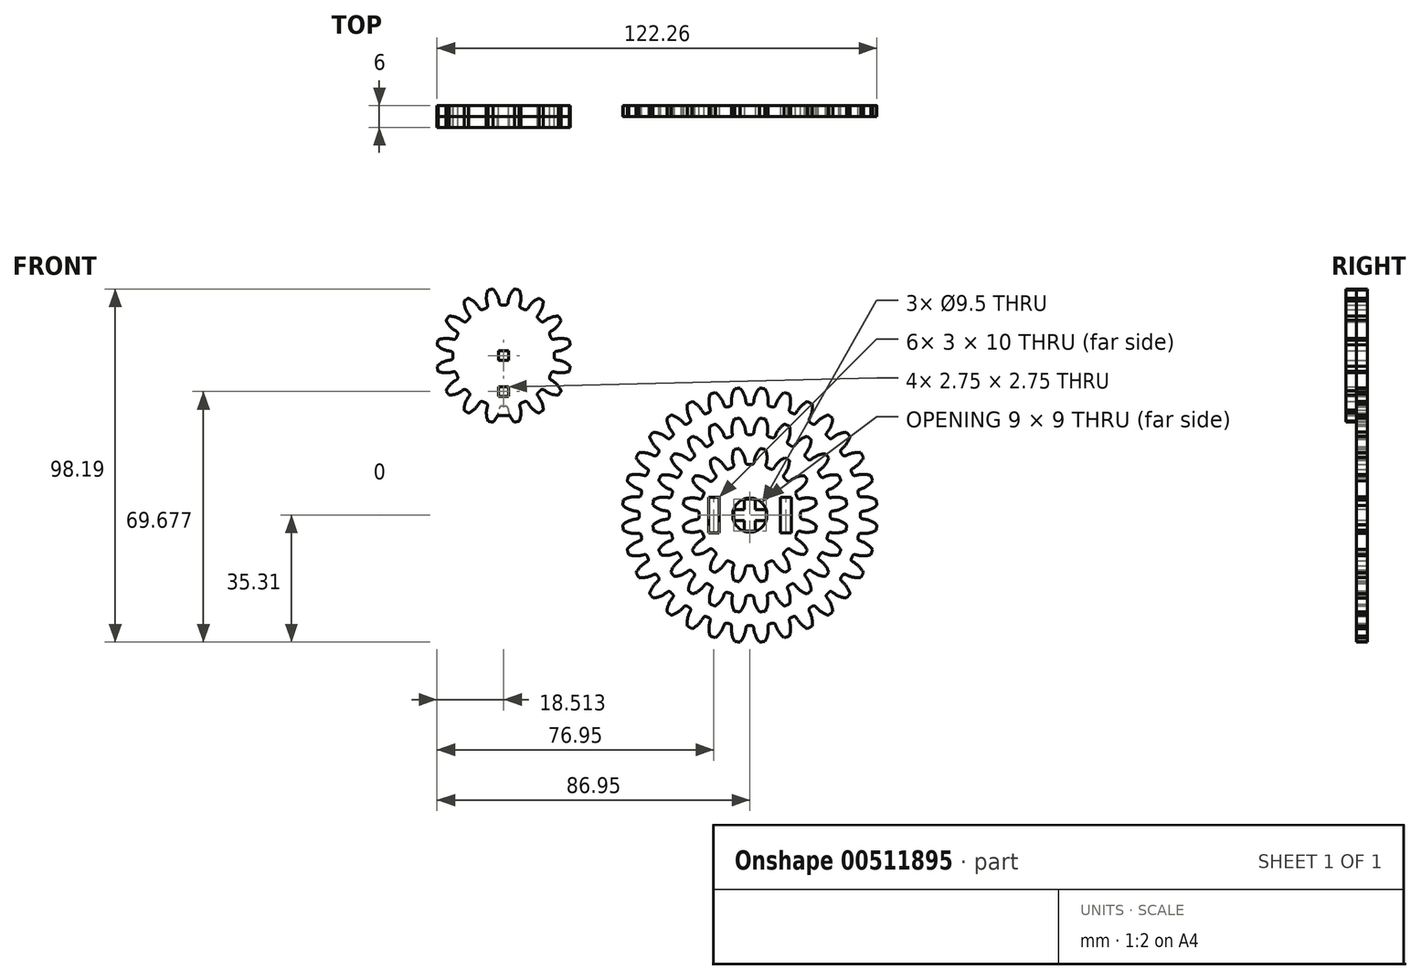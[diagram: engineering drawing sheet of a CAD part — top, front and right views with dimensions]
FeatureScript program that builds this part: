
annotation { "Feature Type Name" : "Feature", "Feature Type Description" : "" }
export const myFeature = defineFeature(function(context is Context, id is Id, definition is map)
    precondition{}
    {
        {
            var Q0;
            Q0=qCreatedBy(makeId("Front.planeOp"),FACE);
            var sketch = newSketch(context, id + "F0", { "sketchPlane" : qUnion([Q0])});
            skArc(sketch, "E0.0", {"start": v(4.27, 26.74) * mm, "mid": v(3.54, 26.85) * mm, "end": v(2.8, 26.94) * mm});
            skArc(sketch, "E1.0", {"start": v(5.4, 21.73) * mm, "mid": v(4.95, 22.07) * mm, "end": v(4.85, 22.62) * mm});
            skArc(sketch, "E2.0", {"start": v(6.18, 21.53) * mm, "mid": v(5.8, 21.63) * mm, "end": v(5.4, 21.73) * mm});
            skArc(sketch, "E3.0", {"start": v(7.1, 22.02) * mm, "mid": v(6.74, 21.58) * mm, "end": v(6.18, 21.53) * mm});
            skPoint(sketch, "E4.0", {"position": v(9.67, 25.3) * mm});
            skArc(sketch, "E5", {"start": v(4.85, 22.62) * mm, "mid": v(4.93, 24.74) * mm, "end": v(4.27, 26.74) * mm});
            skArc(sketch, "E6", {"start": v(7.1, 22.02) * mm, "mid": v(8.1, 23.89) * mm, "end": v(9.67, 25.3) * mm});
            skArc(sketch, "E7.1.0", {"start": v(11.54, 19.2) * mm, "mid": v(11.2, 19.4) * mm, "end": v(10.85, 19.6) * mm});
            skArc(sketch, "E7.1.1", {"start": v(10.85, 19.6) * mm, "mid": v(10.5, 20.03) * mm, "end": v(10.54, 20.6) * mm});
            skPoint(sketch, "E7.1.2", {"position": v(15.9, 21.93) * mm});
            skArc(sketch, "E7.1.3", {"start": v(12.56, 19.43) * mm, "mid": v(12.1, 19.1) * mm, "end": v(11.54, 19.2) * mm});
            skArc(sketch, "E7.1.4", {"start": v(12.56, 19.43) * mm, "mid": v(14, 20.98) * mm, "end": v(15.9, 21.93) * mm});
            skArc(sketch, "E7.1.5", {"start": v(10.54, 20.6) * mm, "mid": v(11.16, 22.62) * mm, "end": v(11.05, 24.73) * mm});
            skArc(sketch, "E7.1.6", {"start": v(11.05, 24.73) * mm, "mid": v(10.36, 25.02) * mm, "end": v(9.67, 25.3) * mm});
            skArc(sketch, "E7.2.0", {"start": v(16.12, 15.55) * mm, "mid": v(15.84, 15.84) * mm, "end": v(15.55, 16.12) * mm});
            skArc(sketch, "E7.2.1", {"start": v(15.55, 16.12) * mm, "mid": v(15.32, 16.63) * mm, "end": v(15.52, 17.16) * mm});
            skPoint(sketch, "E7.2.2", {"position": v(21.03, 17.07) * mm});
            skArc(sketch, "E7.2.3", {"start": v(17.16, 15.52) * mm, "mid": v(16.63, 15.32) * mm, "end": v(16.12, 15.55) * mm});
            skArc(sketch, "E7.2.4", {"start": v(17.16, 15.52) * mm, "mid": v(18.96, 16.64) * mm, "end": v(21.03, 17.07) * mm});
            skArc(sketch, "E7.2.5", {"start": v(15.52, 17.16) * mm, "mid": v(16.64, 18.96) * mm, "end": v(17.07, 21.03) * mm});
            skArc(sketch, "E7.2.6", {"start": v(17.07, 21.03) * mm, "mid": v(16.49, 21.49) * mm, "end": v(15.9, 21.93) * mm});
            skArc(sketch, "E7.3.0", {"start": v(19.6, 10.85) * mm, "mid": v(19.4, 11.2) * mm, "end": v(19.2, 11.54) * mm});
            skArc(sketch, "E7.3.1", {"start": v(19.2, 11.54) * mm, "mid": v(19.1, 12.1) * mm, "end": v(19.43, 12.56) * mm});
            skPoint(sketch, "E7.3.2", {"position": v(24.73, 11.05) * mm});
            skArc(sketch, "E7.3.3", {"start": v(20.6, 10.54) * mm, "mid": v(20.03, 10.5) * mm, "end": v(19.6, 10.85) * mm});
            skArc(sketch, "E7.3.4", {"start": v(20.6, 10.54) * mm, "mid": v(22.62, 11.16) * mm, "end": v(24.73, 11.05) * mm});
            skArc(sketch, "E7.3.5", {"start": v(19.43, 12.56) * mm, "mid": v(20.98, 14) * mm, "end": v(21.93, 15.9) * mm});
            skArc(sketch, "E7.3.6", {"start": v(21.93, 15.9) * mm, "mid": v(21.49, 16.49) * mm, "end": v(21.03, 17.07) * mm});
            skArc(sketch, "E7.4.0", {"start": v(21.73, 5.4) * mm, "mid": v(21.63, 5.8) * mm, "end": v(21.53, 6.18) * mm});
            skArc(sketch, "E7.4.1", {"start": v(21.53, 6.18) * mm, "mid": v(21.58, 6.74) * mm, "end": v(22.02, 7.1) * mm});
            skPoint(sketch, "E7.4.2", {"position": v(26.74, 4.27) * mm});
            skArc(sketch, "E7.4.3", {"start": v(22.62, 4.85) * mm, "mid": v(22.07, 4.95) * mm, "end": v(21.73, 5.4) * mm});
            skArc(sketch, "E7.4.4", {"start": v(22.62, 4.85) * mm, "mid": v(24.74, 4.93) * mm, "end": v(26.74, 4.27) * mm});
            skArc(sketch, "E7.4.5", {"start": v(22.02, 7.1) * mm, "mid": v(23.89, 8.1) * mm, "end": v(25.3, 9.67) * mm});
            skArc(sketch, "E7.4.6", {"start": v(25.3, 9.67) * mm, "mid": v(25.02, 10.36) * mm, "end": v(24.73, 11.05) * mm});
            skArc(sketch, "E7.5.0", {"start": v(22.4, -0.4) * mm, "mid": v(22.4, 0) * mm, "end": v(22.4, 0.4) * mm});
            skArc(sketch, "E7.5.1", {"start": v(22.4, 0.4) * mm, "mid": v(22.6, 0.93) * mm, "end": v(23.1, 1.17) * mm});
            skPoint(sketch, "E7.5.2", {"position": v(26.94, -2.8) * mm});
            skArc(sketch, "E7.5.3", {"start": v(23.1, -1.17) * mm, "mid": v(22.6, -0.93) * mm, "end": v(22.4, -0.4) * mm});
            skArc(sketch, "E7.5.4", {"start": v(23.1, -1.17) * mm, "mid": v(25.17, -1.64) * mm, "end": v(26.94, -2.8) * mm});
            skArc(sketch, "E7.5.5", {"start": v(23.1, 1.17) * mm, "mid": v(25.17, 1.64) * mm, "end": v(26.94, 2.8) * mm});
            skArc(sketch, "E7.5.6", {"start": v(26.94, 2.8) * mm, "mid": v(26.85, 3.54) * mm, "end": v(26.74, 4.27) * mm});
            skArc(sketch, "E7.6.0", {"start": v(21.53, -6.18) * mm, "mid": v(21.63, -5.8) * mm, "end": v(21.73, -5.4) * mm});
            skArc(sketch, "E7.6.1", {"start": v(21.73, -5.4) * mm, "mid": v(22.07, -4.95) * mm, "end": v(22.62, -4.85) * mm});
            skPoint(sketch, "E7.6.2", {"position": v(25.3, -9.67) * mm});
            skArc(sketch, "E7.6.3", {"start": v(22.02, -7.1) * mm, "mid": v(21.58, -6.74) * mm, "end": v(21.53, -6.18) * mm});
            skArc(sketch, "E7.6.4", {"start": v(22.02, -7.1) * mm, "mid": v(23.89, -8.1) * mm, "end": v(25.3, -9.67) * mm});
            skArc(sketch, "E7.6.5", {"start": v(22.62, -4.85) * mm, "mid": v(24.74, -4.93) * mm, "end": v(26.74, -4.27) * mm});
            skArc(sketch, "E7.6.6", {"start": v(26.74, -4.27) * mm, "mid": v(26.85, -3.54) * mm, "end": v(26.94, -2.8) * mm});
            skArc(sketch, "E7.7.0", {"start": v(19.2, -11.54) * mm, "mid": v(19.4, -11.2) * mm, "end": v(19.6, -10.85) * mm});
            skArc(sketch, "E7.7.1", {"start": v(19.6, -10.85) * mm, "mid": v(20.03, -10.5) * mm, "end": v(20.6, -10.54) * mm});
            skPoint(sketch, "E7.7.2", {"position": v(21.93, -15.9) * mm});
            skArc(sketch, "E7.7.3", {"start": v(19.43, -12.56) * mm, "mid": v(19.1, -12.1) * mm, "end": v(19.2, -11.54) * mm});
            skArc(sketch, "E7.7.4", {"start": v(19.43, -12.56) * mm, "mid": v(20.98, -14) * mm, "end": v(21.93, -15.9) * mm});
            skArc(sketch, "E7.7.5", {"start": v(20.6, -10.54) * mm, "mid": v(22.62, -11.16) * mm, "end": v(24.73, -11.05) * mm});
            skArc(sketch, "E7.7.6", {"start": v(24.73, -11.05) * mm, "mid": v(25.02, -10.36) * mm, "end": v(25.3, -9.67) * mm});
            skArc(sketch, "E7.8.0", {"start": v(15.55, -16.12) * mm, "mid": v(15.84, -15.84) * mm, "end": v(16.12, -15.55) * mm});
            skArc(sketch, "E7.8.1", {"start": v(16.12, -15.55) * mm, "mid": v(16.63, -15.32) * mm, "end": v(17.16, -15.52) * mm});
            skPoint(sketch, "E7.8.2", {"position": v(17.07, -21.03) * mm});
            skArc(sketch, "E7.8.3", {"start": v(15.52, -17.16) * mm, "mid": v(15.32, -16.63) * mm, "end": v(15.55, -16.12) * mm});
            skArc(sketch, "E7.8.4", {"start": v(15.52, -17.16) * mm, "mid": v(16.64, -18.96) * mm, "end": v(17.07, -21.03) * mm});
            skArc(sketch, "E7.8.5", {"start": v(17.16, -15.52) * mm, "mid": v(18.96, -16.64) * mm, "end": v(21.03, -17.07) * mm});
            skArc(sketch, "E7.8.6", {"start": v(21.03, -17.07) * mm, "mid": v(21.49, -16.49) * mm, "end": v(21.93, -15.9) * mm});
            skArc(sketch, "E7.9.0", {"start": v(10.85, -19.6) * mm, "mid": v(11.2, -19.4) * mm, "end": v(11.54, -19.2) * mm});
            skArc(sketch, "E7.9.1", {"start": v(11.54, -19.2) * mm, "mid": v(12.1, -19.1) * mm, "end": v(12.56, -19.43) * mm});
            skPoint(sketch, "E7.9.2", {"position": v(11.05, -24.73) * mm});
            skArc(sketch, "E7.9.3", {"start": v(10.54, -20.6) * mm, "mid": v(10.5, -20.03) * mm, "end": v(10.85, -19.6) * mm});
            skArc(sketch, "E7.9.4", {"start": v(10.54, -20.6) * mm, "mid": v(11.16, -22.62) * mm, "end": v(11.05, -24.73) * mm});
            skArc(sketch, "E7.9.5", {"start": v(12.56, -19.43) * mm, "mid": v(14, -20.98) * mm, "end": v(15.9, -21.93) * mm});
            skArc(sketch, "E7.9.6", {"start": v(15.9, -21.93) * mm, "mid": v(16.49, -21.49) * mm, "end": v(17.07, -21.03) * mm});
            skArc(sketch, "E7.10.0", {"start": v(5.4, -21.73) * mm, "mid": v(5.8, -21.63) * mm, "end": v(6.18, -21.53) * mm});
            skArc(sketch, "E7.10.1", {"start": v(6.18, -21.53) * mm, "mid": v(6.74, -21.58) * mm, "end": v(7.1, -22.02) * mm});
            skPoint(sketch, "E7.10.2", {"position": v(4.27, -26.74) * mm});
            skArc(sketch, "E7.10.3", {"start": v(4.85, -22.62) * mm, "mid": v(4.95, -22.07) * mm, "end": v(5.4, -21.73) * mm});
            skArc(sketch, "E7.10.4", {"start": v(4.85, -22.62) * mm, "mid": v(4.93, -24.74) * mm, "end": v(4.27, -26.74) * mm});
            skArc(sketch, "E7.10.5", {"start": v(7.1, -22.02) * mm, "mid": v(8.1, -23.89) * mm, "end": v(9.67, -25.3) * mm});
            skArc(sketch, "E7.10.6", {"start": v(9.67, -25.3) * mm, "mid": v(10.36, -25.02) * mm, "end": v(11.05, -24.73) * mm});
            skArc(sketch, "E7.11.0", {"start": v(-0.4, -22.4) * mm, "mid": v(0, -22.4) * mm, "end": v(0.4, -22.4) * mm});
            skArc(sketch, "E7.11.1", {"start": v(0.4, -22.4) * mm, "mid": v(0.93, -22.6) * mm, "end": v(1.17, -23.1) * mm});
            skPoint(sketch, "E7.11.2", {"position": v(-2.8, -26.94) * mm});
            skArc(sketch, "E7.11.3", {"start": v(-1.17, -23.1) * mm, "mid": v(-0.93, -22.6) * mm, "end": v(-0.4, -22.4) * mm});
            skArc(sketch, "E7.11.4", {"start": v(-1.17, -23.1) * mm, "mid": v(-1.64, -25.17) * mm, "end": v(-2.8, -26.94) * mm});
            skArc(sketch, "E7.11.5", {"start": v(1.17, -23.1) * mm, "mid": v(1.64, -25.17) * mm, "end": v(2.8, -26.94) * mm});
            skArc(sketch, "E7.11.6", {"start": v(2.8, -26.94) * mm, "mid": v(3.54, -26.85) * mm, "end": v(4.27, -26.74) * mm});
            skArc(sketch, "E7.12.0", {"start": v(-6.18, -21.53) * mm, "mid": v(-5.8, -21.63) * mm, "end": v(-5.4, -21.73) * mm});
            skArc(sketch, "E7.12.1", {"start": v(-5.4, -21.73) * mm, "mid": v(-4.95, -22.07) * mm, "end": v(-4.85, -22.62) * mm});
            skPoint(sketch, "E7.12.2", {"position": v(-9.67, -25.3) * mm});
            skArc(sketch, "E7.12.3", {"start": v(-7.1, -22.02) * mm, "mid": v(-6.74, -21.58) * mm, "end": v(-6.18, -21.53) * mm});
            skArc(sketch, "E7.12.4", {"start": v(-7.1, -22.02) * mm, "mid": v(-8.1, -23.89) * mm, "end": v(-9.67, -25.3) * mm});
            skArc(sketch, "E7.12.5", {"start": v(-4.85, -22.62) * mm, "mid": v(-4.93, -24.74) * mm, "end": v(-4.27, -26.74) * mm});
            skArc(sketch, "E7.12.6", {"start": v(-4.27, -26.74) * mm, "mid": v(-3.54, -26.85) * mm, "end": v(-2.8, -26.94) * mm});
            skArc(sketch, "E7.13.0", {"start": v(-11.54, -19.2) * mm, "mid": v(-11.2, -19.4) * mm, "end": v(-10.85, -19.6) * mm});
            skArc(sketch, "E7.13.1", {"start": v(-10.85, -19.6) * mm, "mid": v(-10.5, -20.03) * mm, "end": v(-10.54, -20.6) * mm});
            skPoint(sketch, "E7.13.2", {"position": v(-15.9, -21.93) * mm});
            skArc(sketch, "E7.13.3", {"start": v(-12.56, -19.43) * mm, "mid": v(-12.1, -19.1) * mm, "end": v(-11.54, -19.2) * mm});
            skArc(sketch, "E7.13.4", {"start": v(-12.56, -19.43) * mm, "mid": v(-14, -20.98) * mm, "end": v(-15.9, -21.93) * mm});
            skArc(sketch, "E7.13.5", {"start": v(-10.54, -20.6) * mm, "mid": v(-11.16, -22.62) * mm, "end": v(-11.05, -24.73) * mm});
            skArc(sketch, "E7.13.6", {"start": v(-11.05, -24.73) * mm, "mid": v(-10.36, -25.02) * mm, "end": v(-9.67, -25.3) * mm});
            skArc(sketch, "E7.14.0", {"start": v(-16.12, -15.55) * mm, "mid": v(-15.84, -15.84) * mm, "end": v(-15.55, -16.12) * mm});
            skArc(sketch, "E7.14.1", {"start": v(-15.55, -16.12) * mm, "mid": v(-15.32, -16.63) * mm, "end": v(-15.52, -17.16) * mm});
            skPoint(sketch, "E7.14.2", {"position": v(-21.03, -17.07) * mm});
            skArc(sketch, "E7.14.3", {"start": v(-17.16, -15.52) * mm, "mid": v(-16.63, -15.32) * mm, "end": v(-16.12, -15.55) * mm});
            skArc(sketch, "E7.14.4", {"start": v(-17.16, -15.52) * mm, "mid": v(-18.96, -16.64) * mm, "end": v(-21.03, -17.07) * mm});
            skArc(sketch, "E7.14.5", {"start": v(-15.52, -17.16) * mm, "mid": v(-16.64, -18.96) * mm, "end": v(-17.07, -21.03) * mm});
            skArc(sketch, "E7.14.6", {"start": v(-17.07, -21.03) * mm, "mid": v(-16.49, -21.49) * mm, "end": v(-15.9, -21.93) * mm});
            skArc(sketch, "E7.15.0", {"start": v(-19.6, -10.85) * mm, "mid": v(-19.4, -11.2) * mm, "end": v(-19.2, -11.54) * mm});
            skArc(sketch, "E7.15.1", {"start": v(-19.2, -11.54) * mm, "mid": v(-19.1, -12.1) * mm, "end": v(-19.43, -12.56) * mm});
            skPoint(sketch, "E7.15.2", {"position": v(-24.73, -11.05) * mm});
            skArc(sketch, "E7.15.3", {"start": v(-20.6, -10.54) * mm, "mid": v(-20.03, -10.5) * mm, "end": v(-19.6, -10.85) * mm});
            skArc(sketch, "E7.15.4", {"start": v(-20.6, -10.54) * mm, "mid": v(-22.62, -11.16) * mm, "end": v(-24.73, -11.05) * mm});
            skArc(sketch, "E7.15.5", {"start": v(-19.43, -12.56) * mm, "mid": v(-20.98, -14) * mm, "end": v(-21.93, -15.9) * mm});
            skArc(sketch, "E7.15.6", {"start": v(-21.93, -15.9) * mm, "mid": v(-21.49, -16.49) * mm, "end": v(-21.03, -17.07) * mm});
            skArc(sketch, "E7.16.0", {"start": v(-21.73, -5.4) * mm, "mid": v(-21.63, -5.8) * mm, "end": v(-21.53, -6.18) * mm});
            skArc(sketch, "E7.16.1", {"start": v(-21.53, -6.18) * mm, "mid": v(-21.58, -6.74) * mm, "end": v(-22.02, -7.1) * mm});
            skPoint(sketch, "E7.16.2", {"position": v(-26.74, -4.27) * mm});
            skArc(sketch, "E7.16.3", {"start": v(-22.62, -4.85) * mm, "mid": v(-22.07, -4.95) * mm, "end": v(-21.73, -5.4) * mm});
            skArc(sketch, "E7.16.4", {"start": v(-22.62, -4.85) * mm, "mid": v(-24.74, -4.93) * mm, "end": v(-26.74, -4.27) * mm});
            skArc(sketch, "E7.16.5", {"start": v(-22.02, -7.1) * mm, "mid": v(-23.89, -8.1) * mm, "end": v(-25.3, -9.67) * mm});
            skArc(sketch, "E7.16.6", {"start": v(-25.3, -9.67) * mm, "mid": v(-25.02, -10.36) * mm, "end": v(-24.73, -11.05) * mm});
            skArc(sketch, "E7.17.0", {"start": v(-22.4, 0.4) * mm, "mid": v(-22.4, 0) * mm, "end": v(-22.4, -0.4) * mm});
            skArc(sketch, "E7.17.1", {"start": v(-22.4, -0.4) * mm, "mid": v(-22.6, -0.93) * mm, "end": v(-23.1, -1.17) * mm});
            skPoint(sketch, "E7.17.2", {"position": v(-26.94, 2.8) * mm});
            skArc(sketch, "E7.17.3", {"start": v(-23.1, 1.17) * mm, "mid": v(-22.6, 0.93) * mm, "end": v(-22.4, 0.4) * mm});
            skArc(sketch, "E7.17.4", {"start": v(-23.1, 1.17) * mm, "mid": v(-25.17, 1.64) * mm, "end": v(-26.94, 2.8) * mm});
            skArc(sketch, "E7.17.5", {"start": v(-23.1, -1.17) * mm, "mid": v(-25.17, -1.64) * mm, "end": v(-26.94, -2.8) * mm});
            skArc(sketch, "E7.17.6", {"start": v(-26.94, -2.8) * mm, "mid": v(-26.85, -3.54) * mm, "end": v(-26.74, -4.27) * mm});
            skArc(sketch, "E7.18.0", {"start": v(-21.53, 6.18) * mm, "mid": v(-21.63, 5.8) * mm, "end": v(-21.73, 5.4) * mm});
            skArc(sketch, "E7.18.1", {"start": v(-21.73, 5.4) * mm, "mid": v(-22.07, 4.95) * mm, "end": v(-22.62, 4.85) * mm});
            skPoint(sketch, "E7.18.2", {"position": v(-25.3, 9.67) * mm});
            skArc(sketch, "E7.18.3", {"start": v(-22.02, 7.1) * mm, "mid": v(-21.58, 6.74) * mm, "end": v(-21.53, 6.18) * mm});
            skArc(sketch, "E7.18.4", {"start": v(-22.02, 7.1) * mm, "mid": v(-23.89, 8.1) * mm, "end": v(-25.3, 9.67) * mm});
            skArc(sketch, "E7.18.5", {"start": v(-22.62, 4.85) * mm, "mid": v(-24.74, 4.93) * mm, "end": v(-26.74, 4.27) * mm});
            skArc(sketch, "E7.18.6", {"start": v(-26.74, 4.27) * mm, "mid": v(-26.85, 3.54) * mm, "end": v(-26.94, 2.8) * mm});
            skArc(sketch, "E7.19.0", {"start": v(-19.2, 11.54) * mm, "mid": v(-19.4, 11.2) * mm, "end": v(-19.6, 10.85) * mm});
            skArc(sketch, "E7.19.1", {"start": v(-19.6, 10.85) * mm, "mid": v(-20.03, 10.5) * mm, "end": v(-20.6, 10.54) * mm});
            skPoint(sketch, "E7.19.2", {"position": v(-21.93, 15.9) * mm});
            skArc(sketch, "E7.19.3", {"start": v(-19.43, 12.56) * mm, "mid": v(-19.1, 12.1) * mm, "end": v(-19.2, 11.54) * mm});
            skArc(sketch, "E7.19.4", {"start": v(-19.43, 12.56) * mm, "mid": v(-20.98, 14) * mm, "end": v(-21.93, 15.9) * mm});
            skArc(sketch, "E7.19.5", {"start": v(-20.6, 10.54) * mm, "mid": v(-22.62, 11.16) * mm, "end": v(-24.73, 11.05) * mm});
            skArc(sketch, "E7.19.6", {"start": v(-24.73, 11.05) * mm, "mid": v(-25.02, 10.36) * mm, "end": v(-25.3, 9.67) * mm});
            skArc(sketch, "E7.20.0", {"start": v(-15.55, 16.12) * mm, "mid": v(-15.84, 15.84) * mm, "end": v(-16.12, 15.55) * mm});
            skArc(sketch, "E7.20.1", {"start": v(-16.12, 15.55) * mm, "mid": v(-16.63, 15.32) * mm, "end": v(-17.16, 15.52) * mm});
            skPoint(sketch, "E7.20.2", {"position": v(-17.07, 21.03) * mm});
            skArc(sketch, "E7.20.3", {"start": v(-15.52, 17.16) * mm, "mid": v(-15.32, 16.63) * mm, "end": v(-15.55, 16.12) * mm});
            skArc(sketch, "E7.20.4", {"start": v(-15.52, 17.16) * mm, "mid": v(-16.64, 18.96) * mm, "end": v(-17.07, 21.03) * mm});
            skArc(sketch, "E7.20.5", {"start": v(-17.16, 15.52) * mm, "mid": v(-18.96, 16.64) * mm, "end": v(-21.03, 17.07) * mm});
            skArc(sketch, "E7.20.6", {"start": v(-21.03, 17.07) * mm, "mid": v(-21.49, 16.49) * mm, "end": v(-21.93, 15.9) * mm});
            skArc(sketch, "E7.21.0", {"start": v(-10.85, 19.6) * mm, "mid": v(-11.2, 19.4) * mm, "end": v(-11.54, 19.2) * mm});
            skArc(sketch, "E7.21.1", {"start": v(-11.54, 19.2) * mm, "mid": v(-12.1, 19.1) * mm, "end": v(-12.56, 19.43) * mm});
            skPoint(sketch, "E7.21.2", {"position": v(-11.05, 24.73) * mm});
            skArc(sketch, "E7.21.3", {"start": v(-10.54, 20.6) * mm, "mid": v(-10.5, 20.03) * mm, "end": v(-10.85, 19.6) * mm});
            skArc(sketch, "E7.21.4", {"start": v(-10.54, 20.6) * mm, "mid": v(-11.16, 22.62) * mm, "end": v(-11.05, 24.73) * mm});
            skArc(sketch, "E7.21.5", {"start": v(-12.56, 19.43) * mm, "mid": v(-14, 20.98) * mm, "end": v(-15.9, 21.93) * mm});
            skArc(sketch, "E7.21.6", {"start": v(-15.9, 21.93) * mm, "mid": v(-16.49, 21.49) * mm, "end": v(-17.07, 21.03) * mm});
            skArc(sketch, "E7.22.0", {"start": v(-5.4, 21.73) * mm, "mid": v(-5.8, 21.63) * mm, "end": v(-6.18, 21.53) * mm});
            skArc(sketch, "E7.22.1", {"start": v(-6.18, 21.53) * mm, "mid": v(-6.74, 21.58) * mm, "end": v(-7.1, 22.02) * mm});
            skPoint(sketch, "E7.22.2", {"position": v(-4.27, 26.74) * mm});
            skArc(sketch, "E7.22.3", {"start": v(-4.85, 22.62) * mm, "mid": v(-4.95, 22.07) * mm, "end": v(-5.4, 21.73) * mm});
            skArc(sketch, "E7.22.4", {"start": v(-4.85, 22.62) * mm, "mid": v(-4.93, 24.74) * mm, "end": v(-4.27, 26.74) * mm});
            skArc(sketch, "E7.22.5", {"start": v(-7.1, 22.02) * mm, "mid": v(-8.1, 23.89) * mm, "end": v(-9.67, 25.3) * mm});
            skArc(sketch, "E7.22.6", {"start": v(-9.67, 25.3) * mm, "mid": v(-10.36, 25.02) * mm, "end": v(-11.05, 24.73) * mm});
            skArc(sketch, "E7.23.0", {"start": v(0.4, 22.4) * mm, "mid": v(0, 22.4) * mm, "end": v(-0.4, 22.4) * mm});
            skArc(sketch, "E7.23.1", {"start": v(-0.4, 22.4) * mm, "mid": v(-0.93, 22.6) * mm, "end": v(-1.17, 23.1) * mm});
            skPoint(sketch, "E7.23.2", {"position": v(2.8, 26.94) * mm});
            skArc(sketch, "E7.23.3", {"start": v(1.17, 23.1) * mm, "mid": v(0.93, 22.6) * mm, "end": v(0.4, 22.4) * mm});
            skArc(sketch, "E7.23.4", {"start": v(1.17, 23.1) * mm, "mid": v(1.64, 25.17) * mm, "end": v(2.8, 26.94) * mm});
            skArc(sketch, "E7.23.5", {"start": v(-1.17, 23.1) * mm, "mid": v(-1.64, 25.17) * mm, "end": v(-2.8, 26.94) * mm});
            skArc(sketch, "E7.23.6", {"start": v(-2.8, 26.94) * mm, "mid": v(-3.54, 26.85) * mm, "end": v(-4.27, 26.74) * mm});
            skLineSegment(sketch, "E7.anchor1", {"start": v(0, 0) * mm, "end": v(-1.06, 23.89) * mm, "construction": true});
            skLineSegment(sketch, "E7.anchor2", {"start": v(0, 0) * mm, "end": v(-7.2, 22.8) * mm, "construction": true});
            skLineSegment(sketch, "E8.bottom", {"start": v(1.42, 1.43) * mm, "end": v(-1.43, 1.43) * mm});
            skLineSegment(sketch, "E8.top", {"start": v(1.42, -1.42) * mm, "end": v(-1.43, -1.42) * mm});
            skLineSegment(sketch, "E8.left", {"start": v(1.42, 1.43) * mm, "end": v(1.42, -1.42) * mm});
            skLineSegment(sketch, "E8.right", {"start": v(-1.43, 1.43) * mm, "end": v(-1.43, -1.42) * mm});
            skSolve(sketch);
        }
        {
            var Q0;
            Q0=makeQuery(id+"F0.imprint","IMPRINT",FACE,{"disambiguationData":[TD([[makeQuery(id+"F0.imprint","IMPRINT",EDGE,{"derivedFrom":sQuery(id+"F0.wireOp",EDGE,"E0.0")}),1.0]])]});
            extrude(context, id + "F1", {"entities" : qUnion([Q0]), "depth" : 3 * mm, "offsetDistance" : 25 * mm});
        }
        {
            var Q0;
            Q0=qCreatedBy(makeId("Front.planeOp"),FACE);
            var sketch = newSketch(context, id + "F2", { "sketchPlane" : qUnion([Q0])});
            skArc(sketch, "E9.0", {"start": v(4.33, 18.24) * mm, "mid": v(3.66, 18.39) * mm, "end": v(2.98, 18.51) * mm});
            skArc(sketch, "E10.0", {"start": v(4.98, 13.15) * mm, "mid": v(4.56, 13.54) * mm, "end": v(4.52, 14.12) * mm});
            skArc(sketch, "E11.0", {"start": v(5.78, 12.82) * mm, "mid": v(5.38, 13) * mm, "end": v(4.98, 13.15) * mm});
            skArc(sketch, "E12.0", {"start": v(6.79, 13.18) * mm, "mid": v(6.35, 12.8) * mm, "end": v(5.78, 12.82) * mm});
            skPoint(sketch, "E13.0", {"position": v(9.83, 15.96) * mm});
            skArc(sketch, "E14", {"start": v(4.52, 14.12) * mm, "mid": v(4.8, 16.2) * mm, "end": v(4.33, 18.24) * mm});
            skArc(sketch, "E15", {"start": v(6.79, 13.18) * mm, "mid": v(8.06, 14.84) * mm, "end": v(9.83, 15.96) * mm});
            skArc(sketch, "E16.1.0", {"start": v(11.31, 9.57) * mm, "mid": v(10.77, 9.4) * mm, "end": v(10.24, 9.63) * mm});
            skArc(sketch, "E16.1.1", {"start": v(10.24, 9.63) * mm, "mid": v(9.94, 9.94) * mm, "end": v(9.63, 10.24) * mm});
            skArc(sketch, "E16.1.2", {"start": v(9.57, 11.31) * mm, "mid": v(10.63, 13.13) * mm, "end": v(10.98, 15.2) * mm});
            skArc(sketch, "E16.1.3", {"start": v(11.31, 9.57) * mm, "mid": v(13.13, 10.63) * mm, "end": v(15.2, 10.98) * mm});
            skArc(sketch, "E16.1.4", {"start": v(10.98, 15.2) * mm, "mid": v(10.42, 15.59) * mm, "end": v(9.83, 15.96) * mm});
            skArc(sketch, "E16.1.5", {"start": v(9.63, 10.24) * mm, "mid": v(9.4, 10.77) * mm, "end": v(9.57, 11.31) * mm});
            skPoint(sketch, "E16.1.6", {"position": v(15.2, 10.98) * mm});
            skArc(sketch, "E16.2.0", {"start": v(14.12, 4.52) * mm, "mid": v(13.54, 4.56) * mm, "end": v(13.15, 4.98) * mm});
            skArc(sketch, "E16.2.1", {"start": v(13.15, 4.98) * mm, "mid": v(13, 5.38) * mm, "end": v(12.82, 5.78) * mm});
            skArc(sketch, "E16.2.2", {"start": v(13.18, 6.79) * mm, "mid": v(14.84, 8.06) * mm, "end": v(15.96, 9.83) * mm});
            skArc(sketch, "E16.2.3", {"start": v(14.12, 4.52) * mm, "mid": v(16.2, 4.8) * mm, "end": v(18.24, 4.33) * mm});
            skArc(sketch, "E16.2.4", {"start": v(15.96, 9.83) * mm, "mid": v(15.59, 10.42) * mm, "end": v(15.2, 10.98) * mm});
            skArc(sketch, "E16.2.5", {"start": v(12.82, 5.78) * mm, "mid": v(12.8, 6.35) * mm, "end": v(13.18, 6.79) * mm});
            skPoint(sketch, "E16.2.6", {"position": v(18.24, 4.33) * mm});
            skArc(sketch, "E16.3.0", {"start": v(14.77, -1.23) * mm, "mid": v(14.25, -0.97) * mm, "end": v(14.05, -0.43) * mm});
            skArc(sketch, "E16.3.1", {"start": v(14.05, -0.43) * mm, "mid": v(14.06, 0) * mm, "end": v(14.05, 0.43) * mm});
            skArc(sketch, "E16.3.2", {"start": v(14.77, 1.23) * mm, "mid": v(16.8, 1.77) * mm, "end": v(18.51, 2.98) * mm});
            skArc(sketch, "E16.3.3", {"start": v(14.77, -1.23) * mm, "mid": v(16.8, -1.77) * mm, "end": v(18.51, -2.98) * mm});
            skArc(sketch, "E16.3.4", {"start": v(18.51, 2.98) * mm, "mid": v(18.39, 3.66) * mm, "end": v(18.24, 4.33) * mm});
            skArc(sketch, "E16.3.5", {"start": v(14.05, 0.43) * mm, "mid": v(14.25, 0.97) * mm, "end": v(14.77, 1.23) * mm});
            skPoint(sketch, "E16.3.6", {"position": v(18.51, -2.98) * mm});
            skArc(sketch, "E16.4.0", {"start": v(13.18, -6.79) * mm, "mid": v(12.8, -6.35) * mm, "end": v(12.82, -5.78) * mm});
            skArc(sketch, "E16.4.1", {"start": v(12.82, -5.78) * mm, "mid": v(13, -5.38) * mm, "end": v(13.15, -4.98) * mm});
            skArc(sketch, "E16.4.2", {"start": v(14.12, -4.52) * mm, "mid": v(16.2, -4.8) * mm, "end": v(18.24, -4.33) * mm});
            skArc(sketch, "E16.4.3", {"start": v(13.18, -6.79) * mm, "mid": v(14.84, -8.06) * mm, "end": v(15.96, -9.83) * mm});
            skArc(sketch, "E16.4.4", {"start": v(18.24, -4.33) * mm, "mid": v(18.39, -3.66) * mm, "end": v(18.51, -2.98) * mm});
            skArc(sketch, "E16.4.5", {"start": v(13.15, -4.98) * mm, "mid": v(13.54, -4.56) * mm, "end": v(14.12, -4.52) * mm});
            skPoint(sketch, "E16.4.6", {"position": v(15.96, -9.83) * mm});
            skArc(sketch, "E16.5.0", {"start": v(9.57, -11.31) * mm, "mid": v(9.4, -10.77) * mm, "end": v(9.63, -10.24) * mm});
            skArc(sketch, "E16.5.1", {"start": v(9.63, -10.24) * mm, "mid": v(9.94, -9.94) * mm, "end": v(10.24, -9.63) * mm});
            skArc(sketch, "E16.5.2", {"start": v(11.31, -9.57) * mm, "mid": v(13.13, -10.63) * mm, "end": v(15.2, -10.98) * mm});
            skArc(sketch, "E16.5.3", {"start": v(9.57, -11.31) * mm, "mid": v(10.63, -13.13) * mm, "end": v(10.98, -15.2) * mm});
            skArc(sketch, "E16.5.4", {"start": v(15.2, -10.98) * mm, "mid": v(15.59, -10.42) * mm, "end": v(15.96, -9.83) * mm});
            skArc(sketch, "E16.5.5", {"start": v(10.24, -9.63) * mm, "mid": v(10.77, -9.4) * mm, "end": v(11.31, -9.57) * mm});
            skPoint(sketch, "E16.5.6", {"position": v(10.98, -15.2) * mm});
            skArc(sketch, "E16.6.0", {"start": v(4.52, -14.12) * mm, "mid": v(4.56, -13.54) * mm, "end": v(4.98, -13.15) * mm});
            skArc(sketch, "E16.6.1", {"start": v(4.98, -13.15) * mm, "mid": v(5.38, -13) * mm, "end": v(5.78, -12.82) * mm});
            skArc(sketch, "E16.6.2", {"start": v(6.79, -13.18) * mm, "mid": v(8.06, -14.84) * mm, "end": v(9.83, -15.96) * mm});
            skArc(sketch, "E16.6.3", {"start": v(4.52, -14.12) * mm, "mid": v(4.8, -16.2) * mm, "end": v(4.33, -18.24) * mm});
            skArc(sketch, "E16.6.4", {"start": v(9.83, -15.96) * mm, "mid": v(10.42, -15.59) * mm, "end": v(10.98, -15.2) * mm});
            skArc(sketch, "E16.6.5", {"start": v(5.78, -12.82) * mm, "mid": v(6.35, -12.8) * mm, "end": v(6.79, -13.18) * mm});
            skPoint(sketch, "E16.6.6", {"position": v(4.33, -18.24) * mm});
            skArc(sketch, "E16.7.0", {"start": v(-1.23, -14.77) * mm, "mid": v(-0.97, -14.25) * mm, "end": v(-0.43, -14.05) * mm});
            skArc(sketch, "E16.7.1", {"start": v(-0.43, -14.05) * mm, "mid": v(0, -14.06) * mm, "end": v(0.43, -14.05) * mm});
            skArc(sketch, "E16.7.2", {"start": v(1.23, -14.77) * mm, "mid": v(1.77, -16.8) * mm, "end": v(2.98, -18.51) * mm});
            skArc(sketch, "E16.7.3", {"start": v(-1.23, -14.77) * mm, "mid": v(-1.77, -16.8) * mm, "end": v(-2.98, -18.51) * mm});
            skArc(sketch, "E16.7.4", {"start": v(2.98, -18.51) * mm, "mid": v(3.66, -18.39) * mm, "end": v(4.33, -18.24) * mm});
            skArc(sketch, "E16.7.5", {"start": v(0.43, -14.05) * mm, "mid": v(0.97, -14.25) * mm, "end": v(1.23, -14.77) * mm});
            skPoint(sketch, "E16.7.6", {"position": v(-2.98, -18.51) * mm});
            skArc(sketch, "E16.8.0", {"start": v(-6.79, -13.18) * mm, "mid": v(-6.35, -12.8) * mm, "end": v(-5.78, -12.82) * mm});
            skArc(sketch, "E16.8.1", {"start": v(-5.78, -12.82) * mm, "mid": v(-5.38, -13) * mm, "end": v(-4.98, -13.15) * mm});
            skArc(sketch, "E16.8.2", {"start": v(-4.52, -14.12) * mm, "mid": v(-4.8, -16.2) * mm, "end": v(-4.33, -18.24) * mm});
            skArc(sketch, "E16.8.3", {"start": v(-6.79, -13.18) * mm, "mid": v(-8.06, -14.84) * mm, "end": v(-9.83, -15.96) * mm});
            skArc(sketch, "E16.8.4", {"start": v(-4.33, -18.24) * mm, "mid": v(-3.66, -18.39) * mm, "end": v(-2.98, -18.51) * mm});
            skArc(sketch, "E16.8.5", {"start": v(-4.98, -13.15) * mm, "mid": v(-4.56, -13.54) * mm, "end": v(-4.52, -14.12) * mm});
            skPoint(sketch, "E16.8.6", {"position": v(-9.83, -15.96) * mm});
            skArc(sketch, "E16.9.0", {"start": v(-11.31, -9.57) * mm, "mid": v(-10.77, -9.4) * mm, "end": v(-10.24, -9.63) * mm});
            skArc(sketch, "E16.9.1", {"start": v(-10.24, -9.63) * mm, "mid": v(-9.94, -9.94) * mm, "end": v(-9.63, -10.24) * mm});
            skArc(sketch, "E16.9.2", {"start": v(-9.57, -11.31) * mm, "mid": v(-10.63, -13.13) * mm, "end": v(-10.98, -15.2) * mm});
            skArc(sketch, "E16.9.3", {"start": v(-11.31, -9.57) * mm, "mid": v(-13.13, -10.63) * mm, "end": v(-15.2, -10.98) * mm});
            skArc(sketch, "E16.9.4", {"start": v(-10.98, -15.2) * mm, "mid": v(-10.42, -15.59) * mm, "end": v(-9.83, -15.96) * mm});
            skArc(sketch, "E16.9.5", {"start": v(-9.63, -10.24) * mm, "mid": v(-9.4, -10.77) * mm, "end": v(-9.57, -11.31) * mm});
            skPoint(sketch, "E16.9.6", {"position": v(-15.2, -10.98) * mm});
            skArc(sketch, "E16.10.0", {"start": v(-14.12, -4.52) * mm, "mid": v(-13.54, -4.56) * mm, "end": v(-13.15, -4.98) * mm});
            skArc(sketch, "E16.10.1", {"start": v(-13.15, -4.98) * mm, "mid": v(-13, -5.38) * mm, "end": v(-12.82, -5.78) * mm});
            skArc(sketch, "E16.10.2", {"start": v(-13.18, -6.79) * mm, "mid": v(-14.84, -8.06) * mm, "end": v(-15.96, -9.83) * mm});
            skArc(sketch, "E16.10.3", {"start": v(-14.12, -4.52) * mm, "mid": v(-16.2, -4.8) * mm, "end": v(-18.24, -4.33) * mm});
            skArc(sketch, "E16.10.4", {"start": v(-15.96, -9.83) * mm, "mid": v(-15.59, -10.42) * mm, "end": v(-15.2, -10.98) * mm});
            skArc(sketch, "E16.10.5", {"start": v(-12.82, -5.78) * mm, "mid": v(-12.8, -6.35) * mm, "end": v(-13.18, -6.79) * mm});
            skPoint(sketch, "E16.10.6", {"position": v(-18.24, -4.33) * mm});
            skArc(sketch, "E16.11.0", {"start": v(-14.77, 1.23) * mm, "mid": v(-14.25, 0.97) * mm, "end": v(-14.05, 0.43) * mm});
            skArc(sketch, "E16.11.1", {"start": v(-14.05, 0.43) * mm, "mid": v(-14.06, 0) * mm, "end": v(-14.05, -0.43) * mm});
            skArc(sketch, "E16.11.2", {"start": v(-14.77, -1.23) * mm, "mid": v(-16.8, -1.77) * mm, "end": v(-18.51, -2.98) * mm});
            skArc(sketch, "E16.11.3", {"start": v(-14.77, 1.23) * mm, "mid": v(-16.8, 1.77) * mm, "end": v(-18.51, 2.98) * mm});
            skArc(sketch, "E16.11.4", {"start": v(-18.51, -2.98) * mm, "mid": v(-18.39, -3.66) * mm, "end": v(-18.24, -4.33) * mm});
            skArc(sketch, "E16.11.5", {"start": v(-14.05, -0.43) * mm, "mid": v(-14.25, -0.97) * mm, "end": v(-14.77, -1.23) * mm});
            skPoint(sketch, "E16.11.6", {"position": v(-18.51, 2.98) * mm});
            skArc(sketch, "E16.12.0", {"start": v(-13.18, 6.79) * mm, "mid": v(-12.8, 6.35) * mm, "end": v(-12.82, 5.78) * mm});
            skArc(sketch, "E16.12.1", {"start": v(-12.82, 5.78) * mm, "mid": v(-13, 5.38) * mm, "end": v(-13.15, 4.98) * mm});
            skArc(sketch, "E16.12.2", {"start": v(-14.12, 4.52) * mm, "mid": v(-16.2, 4.8) * mm, "end": v(-18.24, 4.33) * mm});
            skArc(sketch, "E16.12.3", {"start": v(-13.18, 6.79) * mm, "mid": v(-14.84, 8.06) * mm, "end": v(-15.96, 9.83) * mm});
            skArc(sketch, "E16.12.4", {"start": v(-18.24, 4.33) * mm, "mid": v(-18.39, 3.66) * mm, "end": v(-18.51, 2.98) * mm});
            skArc(sketch, "E16.12.5", {"start": v(-13.15, 4.98) * mm, "mid": v(-13.54, 4.56) * mm, "end": v(-14.12, 4.52) * mm});
            skPoint(sketch, "E16.12.6", {"position": v(-15.96, 9.83) * mm});
            skArc(sketch, "E16.13.0", {"start": v(-9.57, 11.31) * mm, "mid": v(-9.4, 10.77) * mm, "end": v(-9.63, 10.24) * mm});
            skArc(sketch, "E16.13.1", {"start": v(-9.63, 10.24) * mm, "mid": v(-9.94, 9.94) * mm, "end": v(-10.24, 9.63) * mm});
            skArc(sketch, "E16.13.2", {"start": v(-11.31, 9.57) * mm, "mid": v(-13.13, 10.63) * mm, "end": v(-15.2, 10.98) * mm});
            skArc(sketch, "E16.13.3", {"start": v(-9.57, 11.31) * mm, "mid": v(-10.63, 13.13) * mm, "end": v(-10.98, 15.2) * mm});
            skArc(sketch, "E16.13.4", {"start": v(-15.2, 10.98) * mm, "mid": v(-15.59, 10.42) * mm, "end": v(-15.96, 9.83) * mm});
            skArc(sketch, "E16.13.5", {"start": v(-10.24, 9.63) * mm, "mid": v(-10.77, 9.4) * mm, "end": v(-11.31, 9.57) * mm});
            skPoint(sketch, "E16.13.6", {"position": v(-10.98, 15.2) * mm});
            skArc(sketch, "E16.14.0", {"start": v(-4.52, 14.12) * mm, "mid": v(-4.56, 13.54) * mm, "end": v(-4.98, 13.15) * mm});
            skArc(sketch, "E16.14.1", {"start": v(-4.98, 13.15) * mm, "mid": v(-5.38, 13) * mm, "end": v(-5.78, 12.82) * mm});
            skArc(sketch, "E16.14.2", {"start": v(-6.79, 13.18) * mm, "mid": v(-8.06, 14.84) * mm, "end": v(-9.83, 15.96) * mm});
            skArc(sketch, "E16.14.3", {"start": v(-4.52, 14.12) * mm, "mid": v(-4.8, 16.2) * mm, "end": v(-4.33, 18.24) * mm});
            skArc(sketch, "E16.14.4", {"start": v(-9.83, 15.96) * mm, "mid": v(-10.42, 15.59) * mm, "end": v(-10.98, 15.2) * mm});
            skArc(sketch, "E16.14.5", {"start": v(-5.78, 12.82) * mm, "mid": v(-6.35, 12.8) * mm, "end": v(-6.79, 13.18) * mm});
            skPoint(sketch, "E16.14.6", {"position": v(-4.33, 18.24) * mm});
            skArc(sketch, "E16.15.0", {"start": v(1.23, 14.77) * mm, "mid": v(0.97, 14.25) * mm, "end": v(0.43, 14.05) * mm});
            skArc(sketch, "E16.15.1", {"start": v(0.43, 14.05) * mm, "mid": v(0, 14.06) * mm, "end": v(-0.43, 14.05) * mm});
            skArc(sketch, "E16.15.2", {"start": v(-1.23, 14.77) * mm, "mid": v(-1.77, 16.8) * mm, "end": v(-2.98, 18.51) * mm});
            skArc(sketch, "E16.15.3", {"start": v(1.23, 14.77) * mm, "mid": v(1.77, 16.8) * mm, "end": v(2.98, 18.51) * mm});
            skArc(sketch, "E16.15.4", {"start": v(-2.98, 18.51) * mm, "mid": v(-3.66, 18.39) * mm, "end": v(-4.33, 18.24) * mm});
            skArc(sketch, "E16.15.5", {"start": v(-0.43, 14.05) * mm, "mid": v(-0.97, 14.25) * mm, "end": v(-1.23, 14.77) * mm});
            skPoint(sketch, "E16.15.6", {"position": v(2.98, 18.51) * mm});
            skLineSegment(sketch, "E16.anchor1", {"start": v(0, 0) * mm, "end": v(-1.13, 15.93) * mm, "construction": true});
            skLineSegment(sketch, "E16.anchor2", {"start": v(0, 0) * mm, "end": v(-7.14, 14.3) * mm, "construction": true});
            skLineSegment(sketch, "E17.bottom", {"start": v(1.38, 1.37) * mm, "end": v(-1.37, 1.38) * mm});
            skLineSegment(sketch, "E17.top", {"start": v(1.37, -1.38) * mm, "end": v(-1.38, -1.38) * mm});
            skLineSegment(sketch, "E17.left", {"start": v(1.38, 1.37) * mm, "end": v(1.37, -1.38) * mm});
            skLineSegment(sketch, "E17.right", {"start": v(-1.37, 1.38) * mm, "end": v(-1.37, -1.37) * mm});
            skSolve(sketch);
        }
        {
            var Q0;
            {var subQ101=sQuery(id+"F2.wireOp",EDGE,"E9.0");Q0=makeQuery(id+"F2.imprint","IMPRINT",FACE,{"disambiguationData":[TD([[makeQuery(id+"F2.imprint","IMPRINT",EDGE,{"derivedFrom":subQ101}),1.0]])]});}
            extrude(context, id + "F3", {"entities" : qUnion([Q0]), "depth" : 3 * mm, "offsetDistance" : 25 * mm});
        }
        {
            var Q0;
            Q0=qCreatedBy(makeId("Front.planeOp"),FACE);
            var sketch = newSketch(context, id + "F4", { "sketchPlane" : qUnion([Q0])});
            skArc(sketch, "E18.0", {"start": v(4.24, 35.16) * mm, "mid": v(3.47, 35.24) * mm, "end": v(2.7, 35.3) * mm});
            skArc(sketch, "E19.0", {"start": v(5.63, 30.2) * mm, "mid": v(5.2, 30.48) * mm, "end": v(5.06, 30.97) * mm});
            skArc(sketch, "E20.0", {"start": v(6.36, 30.06) * mm, "mid": v(6, 30.14) * mm, "end": v(5.63, 30.2) * mm});
            skArc(sketch, "E21.0", {"start": v(7.17, 30.55) * mm, "mid": v(6.86, 30.15) * mm, "end": v(6.36, 30.06) * mm});
            skPoint(sketch, "E22.0", {"position": v(9.54, 34.1) * mm});
            skArc(sketch, "E23", {"start": v(5.06, 30.97) * mm, "mid": v(4.98, 33.13) * mm, "end": v(4.24, 35.16) * mm});
            skArc(sketch, "E24", {"start": v(7.17, 30.55) * mm, "mid": v(8.08, 32.51) * mm, "end": v(9.54, 34.1) * mm});
            skArc(sketch, "E25.1.0", {"start": v(13, 28.57) * mm, "mid": v(14.27, 30.31) * mm, "end": v(16, 31.59) * mm});
            skArc(sketch, "E25.1.1", {"start": v(11, 29.39) * mm, "mid": v(11.34, 31.52) * mm, "end": v(11.02, 33.66) * mm});
            skPoint(sketch, "E25.1.2", {"position": v(16, 31.59) * mm});
            skArc(sketch, "E25.1.3", {"start": v(13, 28.57) * mm, "mid": v(12.61, 28.23) * mm, "end": v(12.1, 28.24) * mm});
            skArc(sketch, "E25.1.4", {"start": v(11.02, 33.66) * mm, "mid": v(10.28, 33.89) * mm, "end": v(9.54, 34.1) * mm});
            skArc(sketch, "E25.1.5", {"start": v(11.42, 28.53) * mm, "mid": v(11.04, 28.88) * mm, "end": v(11, 29.39) * mm});
            skArc(sketch, "E25.1.6", {"start": v(12.1, 28.24) * mm, "mid": v(11.76, 28.39) * mm, "end": v(11.42, 28.53) * mm});
            skArc(sketch, "E25.2.0", {"start": v(18.32, 25.48) * mm, "mid": v(19.9, 26.94) * mm, "end": v(21.86, 27.86) * mm});
            skArc(sketch, "E25.2.1", {"start": v(16.53, 26.68) * mm, "mid": v(17.28, 28.7) * mm, "end": v(17.37, 30.86) * mm});
            skPoint(sketch, "E25.2.2", {"position": v(21.86, 27.86) * mm});
            skArc(sketch, "E25.2.3", {"start": v(18.32, 25.48) * mm, "mid": v(17.88, 25.23) * mm, "end": v(17.38, 25.34) * mm});
            skArc(sketch, "E25.2.4", {"start": v(17.37, 30.86) * mm, "mid": v(16.7, 31.23) * mm, "end": v(16, 31.59) * mm});
            skArc(sketch, "E25.2.5", {"start": v(16.76, 25.75) * mm, "mid": v(16.47, 26.17) * mm, "end": v(16.53, 26.68) * mm});
            skArc(sketch, "E25.2.6", {"start": v(17.38, 25.34) * mm, "mid": v(17.07, 25.55) * mm, "end": v(16.76, 25.75) * mm});
            skArc(sketch, "E25.3.0", {"start": v(22.94, 21.42) * mm, "mid": v(24.78, 22.54) * mm, "end": v(26.88, 23.06) * mm});
            skArc(sketch, "E25.3.1", {"start": v(21.42, 22.94) * mm, "mid": v(22.54, 24.78) * mm, "end": v(23.06, 26.88) * mm});
            skPoint(sketch, "E25.3.2", {"position": v(26.88, 23.06) * mm});
            skArc(sketch, "E25.3.3", {"start": v(22.94, 21.42) * mm, "mid": v(22.45, 21.25) * mm, "end": v(21.99, 21.46) * mm});
            skArc(sketch, "E25.3.4", {"start": v(23.06, 26.88) * mm, "mid": v(22.47, 27.37) * mm, "end": v(21.86, 27.86) * mm});
            skArc(sketch, "E25.3.5", {"start": v(21.46, 21.99) * mm, "mid": v(21.25, 22.45) * mm, "end": v(21.42, 22.94) * mm});
            skArc(sketch, "E25.3.6", {"start": v(21.99, 21.46) * mm, "mid": v(21.73, 21.73) * mm, "end": v(21.46, 21.99) * mm});
            skArc(sketch, "E25.4.0", {"start": v(26.68, 16.53) * mm, "mid": v(28.7, 17.28) * mm, "end": v(30.86, 17.37) * mm});
            skArc(sketch, "E25.4.1", {"start": v(25.48, 18.32) * mm, "mid": v(26.94, 19.9) * mm, "end": v(27.86, 21.86) * mm});
            skPoint(sketch, "E25.4.2", {"position": v(30.86, 17.37) * mm});
            skArc(sketch, "E25.4.3", {"start": v(26.68, 16.53) * mm, "mid": v(26.17, 16.47) * mm, "end": v(25.75, 16.76) * mm});
            skArc(sketch, "E25.4.4", {"start": v(27.86, 21.86) * mm, "mid": v(27.37, 22.47) * mm, "end": v(26.88, 23.06) * mm});
            skArc(sketch, "E25.4.5", {"start": v(25.34, 17.38) * mm, "mid": v(25.23, 17.88) * mm, "end": v(25.48, 18.32) * mm});
            skArc(sketch, "E25.4.6", {"start": v(25.75, 16.76) * mm, "mid": v(25.55, 17.07) * mm, "end": v(25.34, 17.38) * mm});
            skArc(sketch, "E25.5.0", {"start": v(29.39, 11) * mm, "mid": v(31.52, 11.34) * mm, "end": v(33.66, 11.02) * mm});
            skArc(sketch, "E25.5.1", {"start": v(28.57, 13) * mm, "mid": v(30.31, 14.27) * mm, "end": v(31.59, 16) * mm});
            skPoint(sketch, "E25.5.2", {"position": v(33.66, 11.02) * mm});
            skArc(sketch, "E25.5.3", {"start": v(29.39, 11) * mm, "mid": v(28.88, 11.04) * mm, "end": v(28.53, 11.42) * mm});
            skArc(sketch, "E25.5.4", {"start": v(31.59, 16) * mm, "mid": v(31.23, 16.7) * mm, "end": v(30.86, 17.37) * mm});
            skArc(sketch, "E25.5.5", {"start": v(28.24, 12.1) * mm, "mid": v(28.23, 12.61) * mm, "end": v(28.57, 13) * mm});
            skArc(sketch, "E25.5.6", {"start": v(28.53, 11.42) * mm, "mid": v(28.39, 11.76) * mm, "end": v(28.24, 12.1) * mm});
            skArc(sketch, "E25.6.0", {"start": v(30.97, 5.06) * mm, "mid": v(33.13, 4.98) * mm, "end": v(35.16, 4.24) * mm});
            skArc(sketch, "E25.6.1", {"start": v(30.55, 7.17) * mm, "mid": v(32.51, 8.08) * mm, "end": v(34.1, 9.54) * mm});
            skPoint(sketch, "E25.6.2", {"position": v(35.16, 4.24) * mm});
            skArc(sketch, "E25.6.3", {"start": v(30.97, 5.06) * mm, "mid": v(30.48, 5.2) * mm, "end": v(30.2, 5.63) * mm});
            skArc(sketch, "E25.6.4", {"start": v(34.1, 9.54) * mm, "mid": v(33.89, 10.28) * mm, "end": v(33.66, 11.02) * mm});
            skArc(sketch, "E25.6.5", {"start": v(30.06, 6.36) * mm, "mid": v(30.15, 6.86) * mm, "end": v(30.55, 7.17) * mm});
            skArc(sketch, "E25.6.6", {"start": v(30.2, 5.63) * mm, "mid": v(30.14, 6) * mm, "end": v(30.06, 6.36) * mm});
            skArc(sketch, "E25.7.0", {"start": v(31.37, -1.07) * mm, "mid": v(33.46, -1.58) * mm, "end": v(35.3, -2.7) * mm});
            skArc(sketch, "E25.7.1", {"start": v(31.37, 1.07) * mm, "mid": v(33.46, 1.58) * mm, "end": v(35.3, 2.7) * mm});
            skPoint(sketch, "E25.7.2", {"position": v(35.3, -2.7) * mm});
            skArc(sketch, "E25.7.3", {"start": v(31.37, -1.07) * mm, "mid": v(30.9, -0.85) * mm, "end": v(30.72, -0.37) * mm});
            skArc(sketch, "E25.7.4", {"start": v(35.3, 2.7) * mm, "mid": v(35.24, 3.47) * mm, "end": v(35.16, 4.24) * mm});
            skArc(sketch, "E25.7.5", {"start": v(30.72, 0.37) * mm, "mid": v(30.9, 0.85) * mm, "end": v(31.37, 1.07) * mm});
            skArc(sketch, "E25.7.6", {"start": v(30.72, -0.37) * mm, "mid": v(30.73, 0) * mm, "end": v(30.72, 0.37) * mm});
            skArc(sketch, "E25.8.0", {"start": v(30.55, -7.17) * mm, "mid": v(32.51, -8.08) * mm, "end": v(34.1, -9.54) * mm});
            skArc(sketch, "E25.8.1", {"start": v(30.97, -5.06) * mm, "mid": v(33.13, -4.98) * mm, "end": v(35.16, -4.24) * mm});
            skPoint(sketch, "E25.8.2", {"position": v(34.1, -9.54) * mm});
            skArc(sketch, "E25.8.3", {"start": v(30.55, -7.17) * mm, "mid": v(30.15, -6.86) * mm, "end": v(30.06, -6.36) * mm});
            skArc(sketch, "E25.8.4", {"start": v(35.16, -4.24) * mm, "mid": v(35.24, -3.47) * mm, "end": v(35.3, -2.7) * mm});
            skArc(sketch, "E25.8.5", {"start": v(30.2, -5.63) * mm, "mid": v(30.48, -5.2) * mm, "end": v(30.97, -5.06) * mm});
            skArc(sketch, "E25.8.6", {"start": v(30.06, -6.36) * mm, "mid": v(30.14, -6) * mm, "end": v(30.2, -5.63) * mm});
            skArc(sketch, "E25.9.0", {"start": v(28.57, -13) * mm, "mid": v(30.31, -14.27) * mm, "end": v(31.59, -16) * mm});
            skArc(sketch, "E25.9.1", {"start": v(29.39, -11) * mm, "mid": v(31.52, -11.34) * mm, "end": v(33.66, -11.02) * mm});
            skPoint(sketch, "E25.9.2", {"position": v(31.59, -16) * mm});
            skArc(sketch, "E25.9.3", {"start": v(28.57, -13) * mm, "mid": v(28.23, -12.61) * mm, "end": v(28.24, -12.1) * mm});
            skArc(sketch, "E25.9.4", {"start": v(33.66, -11.02) * mm, "mid": v(33.89, -10.28) * mm, "end": v(34.1, -9.54) * mm});
            skArc(sketch, "E25.9.5", {"start": v(28.53, -11.42) * mm, "mid": v(28.88, -11.04) * mm, "end": v(29.39, -11) * mm});
            skArc(sketch, "E25.9.6", {"start": v(28.24, -12.1) * mm, "mid": v(28.39, -11.76) * mm, "end": v(28.53, -11.42) * mm});
            skArc(sketch, "E25.10.0", {"start": v(25.48, -18.32) * mm, "mid": v(26.94, -19.9) * mm, "end": v(27.86, -21.86) * mm});
            skArc(sketch, "E25.10.1", {"start": v(26.68, -16.53) * mm, "mid": v(28.7, -17.28) * mm, "end": v(30.86, -17.37) * mm});
            skPoint(sketch, "E25.10.2", {"position": v(27.86, -21.86) * mm});
            skArc(sketch, "E25.10.3", {"start": v(25.48, -18.32) * mm, "mid": v(25.23, -17.88) * mm, "end": v(25.34, -17.38) * mm});
            skArc(sketch, "E25.10.4", {"start": v(30.86, -17.37) * mm, "mid": v(31.23, -16.7) * mm, "end": v(31.59, -16) * mm});
            skArc(sketch, "E25.10.5", {"start": v(25.75, -16.76) * mm, "mid": v(26.17, -16.47) * mm, "end": v(26.68, -16.53) * mm});
            skArc(sketch, "E25.10.6", {"start": v(25.34, -17.38) * mm, "mid": v(25.55, -17.07) * mm, "end": v(25.75, -16.76) * mm});
            skArc(sketch, "E25.11.0", {"start": v(21.42, -22.94) * mm, "mid": v(22.54, -24.78) * mm, "end": v(23.06, -26.88) * mm});
            skArc(sketch, "E25.11.1", {"start": v(22.94, -21.42) * mm, "mid": v(24.78, -22.54) * mm, "end": v(26.88, -23.06) * mm});
            skPoint(sketch, "E25.11.2", {"position": v(23.06, -26.88) * mm});
            skArc(sketch, "E25.11.3", {"start": v(21.42, -22.94) * mm, "mid": v(21.25, -22.45) * mm, "end": v(21.46, -21.99) * mm});
            skArc(sketch, "E25.11.4", {"start": v(26.88, -23.06) * mm, "mid": v(27.37, -22.47) * mm, "end": v(27.86, -21.86) * mm});
            skArc(sketch, "E25.11.5", {"start": v(21.99, -21.46) * mm, "mid": v(22.45, -21.25) * mm, "end": v(22.94, -21.42) * mm});
            skArc(sketch, "E25.11.6", {"start": v(21.46, -21.99) * mm, "mid": v(21.73, -21.73) * mm, "end": v(21.99, -21.46) * mm});
            skArc(sketch, "E25.12.0", {"start": v(16.53, -26.68) * mm, "mid": v(17.28, -28.7) * mm, "end": v(17.37, -30.86) * mm});
            skArc(sketch, "E25.12.1", {"start": v(18.32, -25.48) * mm, "mid": v(19.9, -26.94) * mm, "end": v(21.86, -27.86) * mm});
            skPoint(sketch, "E25.12.2", {"position": v(17.37, -30.86) * mm});
            skArc(sketch, "E25.12.3", {"start": v(16.53, -26.68) * mm, "mid": v(16.47, -26.17) * mm, "end": v(16.76, -25.75) * mm});
            skArc(sketch, "E25.12.4", {"start": v(21.86, -27.86) * mm, "mid": v(22.47, -27.37) * mm, "end": v(23.06, -26.88) * mm});
            skArc(sketch, "E25.12.5", {"start": v(17.38, -25.34) * mm, "mid": v(17.88, -25.23) * mm, "end": v(18.32, -25.48) * mm});
            skArc(sketch, "E25.12.6", {"start": v(16.76, -25.75) * mm, "mid": v(17.07, -25.55) * mm, "end": v(17.38, -25.34) * mm});
            skArc(sketch, "E25.13.0", {"start": v(11, -29.39) * mm, "mid": v(11.34, -31.52) * mm, "end": v(11.02, -33.66) * mm});
            skArc(sketch, "E25.13.1", {"start": v(13, -28.57) * mm, "mid": v(14.27, -30.31) * mm, "end": v(16, -31.59) * mm});
            skPoint(sketch, "E25.13.2", {"position": v(11.02, -33.66) * mm});
            skArc(sketch, "E25.13.3", {"start": v(11, -29.39) * mm, "mid": v(11.04, -28.88) * mm, "end": v(11.42, -28.53) * mm});
            skArc(sketch, "E25.13.4", {"start": v(16, -31.59) * mm, "mid": v(16.7, -31.23) * mm, "end": v(17.37, -30.86) * mm});
            skArc(sketch, "E25.13.5", {"start": v(12.1, -28.24) * mm, "mid": v(12.61, -28.23) * mm, "end": v(13, -28.57) * mm});
            skArc(sketch, "E25.13.6", {"start": v(11.42, -28.53) * mm, "mid": v(11.76, -28.39) * mm, "end": v(12.1, -28.24) * mm});
            skArc(sketch, "E25.14.0", {"start": v(5.06, -30.97) * mm, "mid": v(4.98, -33.13) * mm, "end": v(4.24, -35.16) * mm});
            skArc(sketch, "E25.14.1", {"start": v(7.17, -30.55) * mm, "mid": v(8.08, -32.51) * mm, "end": v(9.54, -34.1) * mm});
            skPoint(sketch, "E25.14.2", {"position": v(4.24, -35.16) * mm});
            skArc(sketch, "E25.14.3", {"start": v(5.06, -30.97) * mm, "mid": v(5.2, -30.48) * mm, "end": v(5.63, -30.2) * mm});
            skArc(sketch, "E25.14.4", {"start": v(9.54, -34.1) * mm, "mid": v(10.28, -33.89) * mm, "end": v(11.02, -33.66) * mm});
            skArc(sketch, "E25.14.5", {"start": v(6.36, -30.06) * mm, "mid": v(6.86, -30.15) * mm, "end": v(7.17, -30.55) * mm});
            skArc(sketch, "E25.14.6", {"start": v(5.63, -30.2) * mm, "mid": v(6, -30.14) * mm, "end": v(6.36, -30.06) * mm});
            skArc(sketch, "E25.15.0", {"start": v(-1.07, -31.37) * mm, "mid": v(-1.58, -33.46) * mm, "end": v(-2.7, -35.3) * mm});
            skArc(sketch, "E25.15.1", {"start": v(1.07, -31.37) * mm, "mid": v(1.58, -33.46) * mm, "end": v(2.7, -35.3) * mm});
            skPoint(sketch, "E25.15.2", {"position": v(-2.7, -35.3) * mm});
            skArc(sketch, "E25.15.3", {"start": v(-1.07, -31.37) * mm, "mid": v(-0.85, -30.9) * mm, "end": v(-0.37, -30.72) * mm});
            skArc(sketch, "E25.15.4", {"start": v(2.7, -35.3) * mm, "mid": v(3.47, -35.24) * mm, "end": v(4.24, -35.16) * mm});
            skArc(sketch, "E25.15.5", {"start": v(0.37, -30.72) * mm, "mid": v(0.85, -30.9) * mm, "end": v(1.07, -31.37) * mm});
            skArc(sketch, "E25.15.6", {"start": v(-0.37, -30.72) * mm, "mid": v(0, -30.73) * mm, "end": v(0.37, -30.72) * mm});
            skArc(sketch, "E25.16.0", {"start": v(-7.17, -30.55) * mm, "mid": v(-8.08, -32.51) * mm, "end": v(-9.54, -34.1) * mm});
            skArc(sketch, "E25.16.1", {"start": v(-5.06, -30.97) * mm, "mid": v(-4.98, -33.13) * mm, "end": v(-4.24, -35.16) * mm});
            skPoint(sketch, "E25.16.2", {"position": v(-9.54, -34.1) * mm});
            skArc(sketch, "E25.16.3", {"start": v(-7.17, -30.55) * mm, "mid": v(-6.86, -30.15) * mm, "end": v(-6.36, -30.06) * mm});
            skArc(sketch, "E25.16.4", {"start": v(-4.24, -35.16) * mm, "mid": v(-3.47, -35.24) * mm, "end": v(-2.7, -35.3) * mm});
            skArc(sketch, "E25.16.5", {"start": v(-5.63, -30.2) * mm, "mid": v(-5.2, -30.48) * mm, "end": v(-5.06, -30.97) * mm});
            skArc(sketch, "E25.16.6", {"start": v(-6.36, -30.06) * mm, "mid": v(-6, -30.14) * mm, "end": v(-5.63, -30.2) * mm});
            skArc(sketch, "E25.17.0", {"start": v(-13, -28.57) * mm, "mid": v(-14.27, -30.31) * mm, "end": v(-16, -31.59) * mm});
            skArc(sketch, "E25.17.1", {"start": v(-11, -29.39) * mm, "mid": v(-11.34, -31.52) * mm, "end": v(-11.02, -33.66) * mm});
            skPoint(sketch, "E25.17.2", {"position": v(-16, -31.59) * mm});
            skArc(sketch, "E25.17.3", {"start": v(-13, -28.57) * mm, "mid": v(-12.61, -28.23) * mm, "end": v(-12.1, -28.24) * mm});
            skArc(sketch, "E25.17.4", {"start": v(-11.02, -33.66) * mm, "mid": v(-10.28, -33.89) * mm, "end": v(-9.54, -34.1) * mm});
            skArc(sketch, "E25.17.5", {"start": v(-11.42, -28.53) * mm, "mid": v(-11.04, -28.88) * mm, "end": v(-11, -29.39) * mm});
            skArc(sketch, "E25.17.6", {"start": v(-12.1, -28.24) * mm, "mid": v(-11.76, -28.39) * mm, "end": v(-11.42, -28.53) * mm});
            skArc(sketch, "E25.18.0", {"start": v(-18.32, -25.48) * mm, "mid": v(-19.9, -26.94) * mm, "end": v(-21.86, -27.86) * mm});
            skArc(sketch, "E25.18.1", {"start": v(-16.53, -26.68) * mm, "mid": v(-17.28, -28.7) * mm, "end": v(-17.37, -30.86) * mm});
            skPoint(sketch, "E25.18.2", {"position": v(-21.86, -27.86) * mm});
            skArc(sketch, "E25.18.3", {"start": v(-18.32, -25.48) * mm, "mid": v(-17.88, -25.23) * mm, "end": v(-17.38, -25.34) * mm});
            skArc(sketch, "E25.18.4", {"start": v(-17.37, -30.86) * mm, "mid": v(-16.7, -31.23) * mm, "end": v(-16, -31.59) * mm});
            skArc(sketch, "E25.18.5", {"start": v(-16.76, -25.75) * mm, "mid": v(-16.47, -26.17) * mm, "end": v(-16.53, -26.68) * mm});
            skArc(sketch, "E25.18.6", {"start": v(-17.38, -25.34) * mm, "mid": v(-17.07, -25.55) * mm, "end": v(-16.76, -25.75) * mm});
            skArc(sketch, "E25.19.0", {"start": v(-22.94, -21.42) * mm, "mid": v(-24.78, -22.54) * mm, "end": v(-26.88, -23.06) * mm});
            skArc(sketch, "E25.19.1", {"start": v(-21.42, -22.94) * mm, "mid": v(-22.54, -24.78) * mm, "end": v(-23.06, -26.88) * mm});
            skPoint(sketch, "E25.19.2", {"position": v(-26.88, -23.06) * mm});
            skArc(sketch, "E25.19.3", {"start": v(-22.94, -21.42) * mm, "mid": v(-22.45, -21.25) * mm, "end": v(-21.99, -21.46) * mm});
            skArc(sketch, "E25.19.4", {"start": v(-23.06, -26.88) * mm, "mid": v(-22.47, -27.37) * mm, "end": v(-21.86, -27.86) * mm});
            skArc(sketch, "E25.19.5", {"start": v(-21.46, -21.99) * mm, "mid": v(-21.25, -22.45) * mm, "end": v(-21.42, -22.94) * mm});
            skArc(sketch, "E25.19.6", {"start": v(-21.99, -21.46) * mm, "mid": v(-21.73, -21.73) * mm, "end": v(-21.46, -21.99) * mm});
            skArc(sketch, "E25.20.0", {"start": v(-26.68, -16.53) * mm, "mid": v(-28.7, -17.28) * mm, "end": v(-30.86, -17.37) * mm});
            skArc(sketch, "E25.20.1", {"start": v(-25.48, -18.32) * mm, "mid": v(-26.94, -19.9) * mm, "end": v(-27.86, -21.86) * mm});
            skPoint(sketch, "E25.20.2", {"position": v(-30.86, -17.37) * mm});
            skArc(sketch, "E25.20.3", {"start": v(-26.68, -16.53) * mm, "mid": v(-26.17, -16.47) * mm, "end": v(-25.75, -16.76) * mm});
            skArc(sketch, "E25.20.4", {"start": v(-27.86, -21.86) * mm, "mid": v(-27.37, -22.47) * mm, "end": v(-26.88, -23.06) * mm});
            skArc(sketch, "E25.20.5", {"start": v(-25.34, -17.38) * mm, "mid": v(-25.23, -17.88) * mm, "end": v(-25.48, -18.32) * mm});
            skArc(sketch, "E25.20.6", {"start": v(-25.75, -16.76) * mm, "mid": v(-25.55, -17.07) * mm, "end": v(-25.34, -17.38) * mm});
            skArc(sketch, "E25.21.0", {"start": v(-29.39, -11) * mm, "mid": v(-31.52, -11.34) * mm, "end": v(-33.66, -11.02) * mm});
            skArc(sketch, "E25.21.1", {"start": v(-28.57, -13) * mm, "mid": v(-30.31, -14.27) * mm, "end": v(-31.59, -16) * mm});
            skPoint(sketch, "E25.21.2", {"position": v(-33.66, -11.02) * mm});
            skArc(sketch, "E25.21.3", {"start": v(-29.39, -11) * mm, "mid": v(-28.88, -11.04) * mm, "end": v(-28.53, -11.42) * mm});
            skArc(sketch, "E25.21.4", {"start": v(-31.59, -16) * mm, "mid": v(-31.23, -16.7) * mm, "end": v(-30.86, -17.37) * mm});
            skArc(sketch, "E25.21.5", {"start": v(-28.24, -12.1) * mm, "mid": v(-28.23, -12.61) * mm, "end": v(-28.57, -13) * mm});
            skArc(sketch, "E25.21.6", {"start": v(-28.53, -11.42) * mm, "mid": v(-28.39, -11.76) * mm, "end": v(-28.24, -12.1) * mm});
            skArc(sketch, "E25.22.0", {"start": v(-30.97, -5.06) * mm, "mid": v(-33.13, -4.98) * mm, "end": v(-35.16, -4.24) * mm});
            skArc(sketch, "E25.22.1", {"start": v(-30.55, -7.17) * mm, "mid": v(-32.51, -8.08) * mm, "end": v(-34.1, -9.54) * mm});
            skPoint(sketch, "E25.22.2", {"position": v(-35.16, -4.24) * mm});
            skArc(sketch, "E25.22.3", {"start": v(-30.97, -5.06) * mm, "mid": v(-30.48, -5.2) * mm, "end": v(-30.2, -5.63) * mm});
            skArc(sketch, "E25.22.4", {"start": v(-34.1, -9.54) * mm, "mid": v(-33.89, -10.28) * mm, "end": v(-33.66, -11.02) * mm});
            skArc(sketch, "E25.22.5", {"start": v(-30.06, -6.36) * mm, "mid": v(-30.15, -6.86) * mm, "end": v(-30.55, -7.17) * mm});
            skArc(sketch, "E25.22.6", {"start": v(-30.2, -5.63) * mm, "mid": v(-30.14, -6) * mm, "end": v(-30.06, -6.36) * mm});
            skArc(sketch, "E25.23.0", {"start": v(-31.37, 1.07) * mm, "mid": v(-33.46, 1.58) * mm, "end": v(-35.3, 2.7) * mm});
            skArc(sketch, "E25.23.1", {"start": v(-31.37, -1.07) * mm, "mid": v(-33.46, -1.58) * mm, "end": v(-35.3, -2.7) * mm});
            skPoint(sketch, "E25.23.2", {"position": v(-35.3, 2.7) * mm});
            skArc(sketch, "E25.23.3", {"start": v(-31.37, 1.07) * mm, "mid": v(-30.9, 0.85) * mm, "end": v(-30.72, 0.37) * mm});
            skArc(sketch, "E25.23.4", {"start": v(-35.3, -2.7) * mm, "mid": v(-35.24, -3.47) * mm, "end": v(-35.16, -4.24) * mm});
            skArc(sketch, "E25.23.5", {"start": v(-30.72, -0.37) * mm, "mid": v(-30.9, -0.85) * mm, "end": v(-31.37, -1.07) * mm});
            skArc(sketch, "E25.23.6", {"start": v(-30.72, 0.37) * mm, "mid": v(-30.73, 0) * mm, "end": v(-30.72, -0.37) * mm});
            skArc(sketch, "E25.24.0", {"start": v(-30.55, 7.17) * mm, "mid": v(-32.51, 8.08) * mm, "end": v(-34.1, 9.54) * mm});
            skArc(sketch, "E25.24.1", {"start": v(-30.97, 5.06) * mm, "mid": v(-33.13, 4.98) * mm, "end": v(-35.16, 4.24) * mm});
            skPoint(sketch, "E25.24.2", {"position": v(-34.1, 9.54) * mm});
            skArc(sketch, "E25.24.3", {"start": v(-30.55, 7.17) * mm, "mid": v(-30.15, 6.86) * mm, "end": v(-30.06, 6.36) * mm});
            skArc(sketch, "E25.24.4", {"start": v(-35.16, 4.24) * mm, "mid": v(-35.24, 3.47) * mm, "end": v(-35.3, 2.7) * mm});
            skArc(sketch, "E25.24.5", {"start": v(-30.2, 5.63) * mm, "mid": v(-30.48, 5.2) * mm, "end": v(-30.97, 5.06) * mm});
            skArc(sketch, "E25.24.6", {"start": v(-30.06, 6.36) * mm, "mid": v(-30.14, 6) * mm, "end": v(-30.2, 5.63) * mm});
            skArc(sketch, "E25.25.0", {"start": v(-28.57, 13) * mm, "mid": v(-30.31, 14.27) * mm, "end": v(-31.59, 16) * mm});
            skArc(sketch, "E25.25.1", {"start": v(-29.39, 11) * mm, "mid": v(-31.52, 11.34) * mm, "end": v(-33.66, 11.02) * mm});
            skPoint(sketch, "E25.25.2", {"position": v(-31.59, 16) * mm});
            skArc(sketch, "E25.25.3", {"start": v(-28.57, 13) * mm, "mid": v(-28.23, 12.61) * mm, "end": v(-28.24, 12.1) * mm});
            skArc(sketch, "E25.25.4", {"start": v(-33.66, 11.02) * mm, "mid": v(-33.89, 10.28) * mm, "end": v(-34.1, 9.54) * mm});
            skArc(sketch, "E25.25.5", {"start": v(-28.53, 11.42) * mm, "mid": v(-28.88, 11.04) * mm, "end": v(-29.39, 11) * mm});
            skArc(sketch, "E25.25.6", {"start": v(-28.24, 12.1) * mm, "mid": v(-28.39, 11.76) * mm, "end": v(-28.53, 11.42) * mm});
            skArc(sketch, "E25.26.0", {"start": v(-25.48, 18.32) * mm, "mid": v(-26.94, 19.9) * mm, "end": v(-27.86, 21.86) * mm});
            skArc(sketch, "E25.26.1", {"start": v(-26.68, 16.53) * mm, "mid": v(-28.7, 17.28) * mm, "end": v(-30.86, 17.37) * mm});
            skPoint(sketch, "E25.26.2", {"position": v(-27.86, 21.86) * mm});
            skArc(sketch, "E25.26.3", {"start": v(-25.48, 18.32) * mm, "mid": v(-25.23, 17.88) * mm, "end": v(-25.34, 17.38) * mm});
            skArc(sketch, "E25.26.4", {"start": v(-30.86, 17.37) * mm, "mid": v(-31.23, 16.7) * mm, "end": v(-31.59, 16) * mm});
            skArc(sketch, "E25.26.5", {"start": v(-25.75, 16.76) * mm, "mid": v(-26.17, 16.47) * mm, "end": v(-26.68, 16.53) * mm});
            skArc(sketch, "E25.26.6", {"start": v(-25.34, 17.38) * mm, "mid": v(-25.55, 17.07) * mm, "end": v(-25.75, 16.76) * mm});
            skArc(sketch, "E25.27.0", {"start": v(-21.42, 22.94) * mm, "mid": v(-22.54, 24.78) * mm, "end": v(-23.06, 26.88) * mm});
            skArc(sketch, "E25.27.1", {"start": v(-22.94, 21.42) * mm, "mid": v(-24.78, 22.54) * mm, "end": v(-26.88, 23.06) * mm});
            skPoint(sketch, "E25.27.2", {"position": v(-23.06, 26.88) * mm});
            skArc(sketch, "E25.27.3", {"start": v(-21.42, 22.94) * mm, "mid": v(-21.25, 22.45) * mm, "end": v(-21.46, 21.99) * mm});
            skArc(sketch, "E25.27.4", {"start": v(-26.88, 23.06) * mm, "mid": v(-27.37, 22.47) * mm, "end": v(-27.86, 21.86) * mm});
            skArc(sketch, "E25.27.5", {"start": v(-21.99, 21.46) * mm, "mid": v(-22.45, 21.25) * mm, "end": v(-22.94, 21.42) * mm});
            skArc(sketch, "E25.27.6", {"start": v(-21.46, 21.99) * mm, "mid": v(-21.73, 21.73) * mm, "end": v(-21.99, 21.46) * mm});
            skArc(sketch, "E25.28.0", {"start": v(-16.53, 26.68) * mm, "mid": v(-17.28, 28.7) * mm, "end": v(-17.37, 30.86) * mm});
            skArc(sketch, "E25.28.1", {"start": v(-18.32, 25.48) * mm, "mid": v(-19.9, 26.94) * mm, "end": v(-21.86, 27.86) * mm});
            skPoint(sketch, "E25.28.2", {"position": v(-17.37, 30.86) * mm});
            skArc(sketch, "E25.28.3", {"start": v(-16.53, 26.68) * mm, "mid": v(-16.47, 26.17) * mm, "end": v(-16.76, 25.75) * mm});
            skArc(sketch, "E25.28.4", {"start": v(-21.86, 27.86) * mm, "mid": v(-22.47, 27.37) * mm, "end": v(-23.06, 26.88) * mm});
            skArc(sketch, "E25.28.5", {"start": v(-17.38, 25.34) * mm, "mid": v(-17.88, 25.23) * mm, "end": v(-18.32, 25.48) * mm});
            skArc(sketch, "E25.28.6", {"start": v(-16.76, 25.75) * mm, "mid": v(-17.07, 25.55) * mm, "end": v(-17.38, 25.34) * mm});
            skArc(sketch, "E25.29.0", {"start": v(-11, 29.39) * mm, "mid": v(-11.34, 31.52) * mm, "end": v(-11.02, 33.66) * mm});
            skArc(sketch, "E25.29.1", {"start": v(-13, 28.57) * mm, "mid": v(-14.27, 30.31) * mm, "end": v(-16, 31.59) * mm});
            skPoint(sketch, "E25.29.2", {"position": v(-11.02, 33.66) * mm});
            skArc(sketch, "E25.29.3", {"start": v(-11, 29.39) * mm, "mid": v(-11.04, 28.88) * mm, "end": v(-11.42, 28.53) * mm});
            skArc(sketch, "E25.29.4", {"start": v(-16, 31.59) * mm, "mid": v(-16.7, 31.23) * mm, "end": v(-17.37, 30.86) * mm});
            skArc(sketch, "E25.29.5", {"start": v(-12.1, 28.24) * mm, "mid": v(-12.61, 28.23) * mm, "end": v(-13, 28.57) * mm});
            skArc(sketch, "E25.29.6", {"start": v(-11.42, 28.53) * mm, "mid": v(-11.76, 28.39) * mm, "end": v(-12.1, 28.24) * mm});
            skArc(sketch, "E25.30.0", {"start": v(-5.06, 30.97) * mm, "mid": v(-4.98, 33.13) * mm, "end": v(-4.24, 35.16) * mm});
            skArc(sketch, "E25.30.1", {"start": v(-7.17, 30.55) * mm, "mid": v(-8.08, 32.51) * mm, "end": v(-9.54, 34.1) * mm});
            skPoint(sketch, "E25.30.2", {"position": v(-4.24, 35.16) * mm});
            skArc(sketch, "E25.30.3", {"start": v(-5.06, 30.97) * mm, "mid": v(-5.2, 30.48) * mm, "end": v(-5.63, 30.2) * mm});
            skArc(sketch, "E25.30.4", {"start": v(-9.54, 34.1) * mm, "mid": v(-10.28, 33.89) * mm, "end": v(-11.02, 33.66) * mm});
            skArc(sketch, "E25.30.5", {"start": v(-6.36, 30.06) * mm, "mid": v(-6.86, 30.15) * mm, "end": v(-7.17, 30.55) * mm});
            skArc(sketch, "E25.30.6", {"start": v(-5.63, 30.2) * mm, "mid": v(-6, 30.14) * mm, "end": v(-6.36, 30.06) * mm});
            skArc(sketch, "E25.31.0", {"start": v(1.07, 31.37) * mm, "mid": v(1.58, 33.46) * mm, "end": v(2.7, 35.3) * mm});
            skArc(sketch, "E25.31.1", {"start": v(-1.07, 31.37) * mm, "mid": v(-1.58, 33.46) * mm, "end": v(-2.7, 35.3) * mm});
            skPoint(sketch, "E25.31.2", {"position": v(2.7, 35.3) * mm});
            skArc(sketch, "E25.31.3", {"start": v(1.07, 31.37) * mm, "mid": v(0.85, 30.9) * mm, "end": v(0.37, 30.72) * mm});
            skArc(sketch, "E25.31.4", {"start": v(-2.7, 35.3) * mm, "mid": v(-3.47, 35.24) * mm, "end": v(-4.24, 35.16) * mm});
            skArc(sketch, "E25.31.5", {"start": v(-0.37, 30.72) * mm, "mid": v(-0.85, 30.9) * mm, "end": v(-1.07, 31.37) * mm});
            skArc(sketch, "E25.31.6", {"start": v(0.37, 30.72) * mm, "mid": v(0, 30.73) * mm, "end": v(-0.37, 30.72) * mm});
            skLineSegment(sketch, "E25.anchor1", {"start": v(0, 0) * mm, "end": v(-1.94, 31.76) * mm, "construction": true});
            skLineSegment(sketch, "E25.anchor2", {"start": v(0, 0) * mm, "end": v(-8.1, 30.77) * mm, "construction": true});
            skSolve(sketch);
        }
        {
            var Q0;
            Q0=makeQuery(id+"F4.imprint","IMPRINT",FACE,{"disambiguationData":[TD([[makeQuery(id+"F4.imprint","IMPRINT",EDGE,{"derivedFrom":sQuery(id+"F4.wireOp",EDGE,"E18.0")}),1.0]])]});
            extrude(context, id + "F5", {"entities" : qUnion([Q0]), "depth" : 3 * mm, "offsetDistance" : 25 * mm});
        }
        {
            var Q0;
            Q0=makeQuery(id+"F5.opExtrude","CAP_FACE",FACE,{"disambiguationData":[OSD([sQuery(id+"F4.wireOp",EDGE,"E18.0"),sQuery(id+"F4.wireOp",EDGE,"E19.0"),sQuery(id+"F4.wireOp",EDGE,"E20.0"),sQuery(id+"F4.wireOp",EDGE,"E21.0"),sQuery(id+"F4.wireOp",EDGE,"E23"),sQuery(id+"F4.wireOp",EDGE,"E24"),sQuery(id+"F4.wireOp",EDGE,"E25.1.0"),sQuery(id+"F4.wireOp",EDGE,"E25.1.1"),sQuery(id+"F4.wireOp",EDGE,"E25.1.3"),sQuery(id+"F4.wireOp",EDGE,"E25.1.4"),sQuery(id+"F4.wireOp",EDGE,"E25.1.5"),sQuery(id+"F4.wireOp",EDGE,"E25.1.6"),sQuery(id+"F4.wireOp",EDGE,"E25.2.0"),sQuery(id+"F4.wireOp",EDGE,"E25.2.1"),sQuery(id+"F4.wireOp",EDGE,"E25.2.3"),sQuery(id+"F4.wireOp",EDGE,"E25.2.4"),sQuery(id+"F4.wireOp",EDGE,"E25.2.5"),sQuery(id+"F4.wireOp",EDGE,"E25.2.6"),sQuery(id+"F4.wireOp",EDGE,"E25.3.0"),sQuery(id+"F4.wireOp",EDGE,"E25.3.1"),sQuery(id+"F4.wireOp",EDGE,"E25.3.3"),sQuery(id+"F4.wireOp",EDGE,"E25.3.4"),sQuery(id+"F4.wireOp",EDGE,"E25.3.5"),sQuery(id+"F4.wireOp",EDGE,"E25.3.6"),sQuery(id+"F4.wireOp",EDGE,"E25.4.0"),sQuery(id+"F4.wireOp",EDGE,"E25.4.1"),sQuery(id+"F4.wireOp",EDGE,"E25.4.3"),sQuery(id+"F4.wireOp",EDGE,"E25.4.4"),sQuery(id+"F4.wireOp",EDGE,"E25.4.5"),sQuery(id+"F4.wireOp",EDGE,"E25.4.6"),sQuery(id+"F4.wireOp",EDGE,"E25.5.0"),sQuery(id+"F4.wireOp",EDGE,"E25.5.1"),sQuery(id+"F4.wireOp",EDGE,"E25.5.3"),sQuery(id+"F4.wireOp",EDGE,"E25.5.4"),sQuery(id+"F4.wireOp",EDGE,"E25.5.5"),sQuery(id+"F4.wireOp",EDGE,"E25.5.6"),sQuery(id+"F4.wireOp",EDGE,"E25.6.0"),sQuery(id+"F4.wireOp",EDGE,"E25.6.1"),sQuery(id+"F4.wireOp",EDGE,"E25.6.3"),sQuery(id+"F4.wireOp",EDGE,"E25.6.4"),sQuery(id+"F4.wireOp",EDGE,"E25.6.5"),sQuery(id+"F4.wireOp",EDGE,"E25.6.6"),sQuery(id+"F4.wireOp",EDGE,"E25.7.0"),sQuery(id+"F4.wireOp",EDGE,"E25.7.1"),sQuery(id+"F4.wireOp",EDGE,"E25.7.3"),sQuery(id+"F4.wireOp",EDGE,"E25.7.4"),sQuery(id+"F4.wireOp",EDGE,"E25.7.5"),sQuery(id+"F4.wireOp",EDGE,"E25.7.6"),sQuery(id+"F4.wireOp",EDGE,"E25.8.0"),sQuery(id+"F4.wireOp",EDGE,"E25.8.1"),sQuery(id+"F4.wireOp",EDGE,"E25.8.3"),sQuery(id+"F4.wireOp",EDGE,"E25.8.4"),sQuery(id+"F4.wireOp",EDGE,"E25.8.5"),sQuery(id+"F4.wireOp",EDGE,"E25.8.6"),sQuery(id+"F4.wireOp",EDGE,"E25.9.0"),sQuery(id+"F4.wireOp",EDGE,"E25.9.1"),sQuery(id+"F4.wireOp",EDGE,"E25.9.3"),sQuery(id+"F4.wireOp",EDGE,"E25.9.4"),sQuery(id+"F4.wireOp",EDGE,"E25.9.5"),sQuery(id+"F4.wireOp",EDGE,"E25.9.6"),sQuery(id+"F4.wireOp",EDGE,"E25.10.0"),sQuery(id+"F4.wireOp",EDGE,"E25.10.1"),sQuery(id+"F4.wireOp",EDGE,"E25.10.3"),sQuery(id+"F4.wireOp",EDGE,"E25.10.4"),sQuery(id+"F4.wireOp",EDGE,"E25.10.5"),sQuery(id+"F4.wireOp",EDGE,"E25.10.6"),sQuery(id+"F4.wireOp",EDGE,"E25.11.0"),sQuery(id+"F4.wireOp",EDGE,"E25.11.1"),sQuery(id+"F4.wireOp",EDGE,"E25.11.3"),sQuery(id+"F4.wireOp",EDGE,"E25.11.4"),sQuery(id+"F4.wireOp",EDGE,"E25.11.5"),sQuery(id+"F4.wireOp",EDGE,"E25.11.6"),sQuery(id+"F4.wireOp",EDGE,"E25.12.0"),sQuery(id+"F4.wireOp",EDGE,"E25.12.1"),sQuery(id+"F4.wireOp",EDGE,"E25.12.3"),sQuery(id+"F4.wireOp",EDGE,"E25.12.4"),sQuery(id+"F4.wireOp",EDGE,"E25.12.5"),sQuery(id+"F4.wireOp",EDGE,"E25.12.6"),sQuery(id+"F4.wireOp",EDGE,"E25.13.0"),sQuery(id+"F4.wireOp",EDGE,"E25.13.1"),sQuery(id+"F4.wireOp",EDGE,"E25.13.3"),sQuery(id+"F4.wireOp",EDGE,"E25.13.4"),sQuery(id+"F4.wireOp",EDGE,"E25.13.5"),sQuery(id+"F4.wireOp",EDGE,"E25.13.6"),sQuery(id+"F4.wireOp",EDGE,"E25.14.0"),sQuery(id+"F4.wireOp",EDGE,"E25.14.1"),sQuery(id+"F4.wireOp",EDGE,"E25.14.3"),sQuery(id+"F4.wireOp",EDGE,"E25.14.4"),sQuery(id+"F4.wireOp",EDGE,"E25.14.5"),sQuery(id+"F4.wireOp",EDGE,"E25.14.6"),sQuery(id+"F4.wireOp",EDGE,"E25.15.0"),sQuery(id+"F4.wireOp",EDGE,"E25.15.1"),sQuery(id+"F4.wireOp",EDGE,"E25.15.3"),sQuery(id+"F4.wireOp",EDGE,"E25.15.4"),sQuery(id+"F4.wireOp",EDGE,"E25.15.5"),sQuery(id+"F4.wireOp",EDGE,"E25.15.6"),sQuery(id+"F4.wireOp",EDGE,"E25.16.0"),sQuery(id+"F4.wireOp",EDGE,"E25.16.1"),sQuery(id+"F4.wireOp",EDGE,"E25.16.3"),sQuery(id+"F4.wireOp",EDGE,"E25.16.4"),sQuery(id+"F4.wireOp",EDGE,"E25.16.5"),sQuery(id+"F4.wireOp",EDGE,"E25.16.6"),sQuery(id+"F4.wireOp",EDGE,"E25.17.0"),sQuery(id+"F4.wireOp",EDGE,"E25.17.1"),sQuery(id+"F4.wireOp",EDGE,"E25.17.3"),sQuery(id+"F4.wireOp",EDGE,"E25.17.4"),sQuery(id+"F4.wireOp",EDGE,"E25.17.5"),sQuery(id+"F4.wireOp",EDGE,"E25.17.6"),sQuery(id+"F4.wireOp",EDGE,"E25.18.0"),sQuery(id+"F4.wireOp",EDGE,"E25.18.1"),sQuery(id+"F4.wireOp",EDGE,"E25.18.3"),sQuery(id+"F4.wireOp",EDGE,"E25.18.4"),sQuery(id+"F4.wireOp",EDGE,"E25.18.5"),sQuery(id+"F4.wireOp",EDGE,"E25.18.6"),sQuery(id+"F4.wireOp",EDGE,"E25.19.0"),sQuery(id+"F4.wireOp",EDGE,"E25.19.1"),sQuery(id+"F4.wireOp",EDGE,"E25.19.3"),sQuery(id+"F4.wireOp",EDGE,"E25.19.4"),sQuery(id+"F4.wireOp",EDGE,"E25.19.5"),sQuery(id+"F4.wireOp",EDGE,"E25.19.6"),sQuery(id+"F4.wireOp",EDGE,"E25.20.0"),sQuery(id+"F4.wireOp",EDGE,"E25.20.1"),sQuery(id+"F4.wireOp",EDGE,"E25.20.3"),sQuery(id+"F4.wireOp",EDGE,"E25.20.4"),sQuery(id+"F4.wireOp",EDGE,"E25.20.5"),sQuery(id+"F4.wireOp",EDGE,"E25.20.6"),sQuery(id+"F4.wireOp",EDGE,"E25.21.0"),sQuery(id+"F4.wireOp",EDGE,"E25.21.1"),sQuery(id+"F4.wireOp",EDGE,"E25.21.3"),sQuery(id+"F4.wireOp",EDGE,"E25.21.4"),sQuery(id+"F4.wireOp",EDGE,"E25.21.5"),sQuery(id+"F4.wireOp",EDGE,"E25.21.6"),sQuery(id+"F4.wireOp",EDGE,"E25.22.0"),sQuery(id+"F4.wireOp",EDGE,"E25.22.1"),sQuery(id+"F4.wireOp",EDGE,"E25.22.3"),sQuery(id+"F4.wireOp",EDGE,"E25.22.4"),sQuery(id+"F4.wireOp",EDGE,"E25.22.5"),sQuery(id+"F4.wireOp",EDGE,"E25.22.6"),sQuery(id+"F4.wireOp",EDGE,"E25.23.0"),sQuery(id+"F4.wireOp",EDGE,"E25.23.1"),sQuery(id+"F4.wireOp",EDGE,"E25.23.3"),sQuery(id+"F4.wireOp",EDGE,"E25.23.4"),sQuery(id+"F4.wireOp",EDGE,"E25.23.5"),sQuery(id+"F4.wireOp",EDGE,"E25.23.6"),sQuery(id+"F4.wireOp",EDGE,"E25.24.0"),sQuery(id+"F4.wireOp",EDGE,"E25.24.1"),sQuery(id+"F4.wireOp",EDGE,"E25.24.3"),sQuery(id+"F4.wireOp",EDGE,"E25.24.4"),sQuery(id+"F4.wireOp",EDGE,"E25.24.5"),sQuery(id+"F4.wireOp",EDGE,"E25.24.6"),sQuery(id+"F4.wireOp",EDGE,"E25.25.0"),sQuery(id+"F4.wireOp",EDGE,"E25.25.1"),sQuery(id+"F4.wireOp",EDGE,"E25.25.3"),sQuery(id+"F4.wireOp",EDGE,"E25.25.4"),sQuery(id+"F4.wireOp",EDGE,"E25.25.5"),sQuery(id+"F4.wireOp",EDGE,"E25.25.6"),sQuery(id+"F4.wireOp",EDGE,"E25.26.0"),sQuery(id+"F4.wireOp",EDGE,"E25.26.1"),sQuery(id+"F4.wireOp",EDGE,"E25.26.3"),sQuery(id+"F4.wireOp",EDGE,"E25.26.4"),sQuery(id+"F4.wireOp",EDGE,"E25.26.5"),sQuery(id+"F4.wireOp",EDGE,"E25.26.6"),sQuery(id+"F4.wireOp",EDGE,"E25.27.0"),sQuery(id+"F4.wireOp",EDGE,"E25.27.1"),sQuery(id+"F4.wireOp",EDGE,"E25.27.3"),sQuery(id+"F4.wireOp",EDGE,"E25.27.4"),sQuery(id+"F4.wireOp",EDGE,"E25.27.5"),sQuery(id+"F4.wireOp",EDGE,"E25.27.6"),sQuery(id+"F4.wireOp",EDGE,"E25.28.0"),sQuery(id+"F4.wireOp",EDGE,"E25.28.1"),sQuery(id+"F4.wireOp",EDGE,"E25.28.3"),sQuery(id+"F4.wireOp",EDGE,"E25.28.4"),sQuery(id+"F4.wireOp",EDGE,"E25.28.5"),sQuery(id+"F4.wireOp",EDGE,"E25.28.6"),sQuery(id+"F4.wireOp",EDGE,"E25.29.0"),sQuery(id+"F4.wireOp",EDGE,"E25.29.1"),sQuery(id+"F4.wireOp",EDGE,"E25.29.3"),sQuery(id+"F4.wireOp",EDGE,"E25.29.4"),sQuery(id+"F4.wireOp",EDGE,"E25.29.5"),sQuery(id+"F4.wireOp",EDGE,"E25.29.6"),sQuery(id+"F4.wireOp",EDGE,"E25.30.0"),sQuery(id+"F4.wireOp",EDGE,"E25.30.1"),sQuery(id+"F4.wireOp",EDGE,"E25.30.3"),sQuery(id+"F4.wireOp",EDGE,"E25.30.4"),sQuery(id+"F4.wireOp",EDGE,"E25.30.5"),sQuery(id+"F4.wireOp",EDGE,"E25.30.6"),sQuery(id+"F4.wireOp",EDGE,"E25.31.0"),sQuery(id+"F4.wireOp",EDGE,"E25.31.1"),sQuery(id+"F4.wireOp",EDGE,"E25.31.3"),sQuery(id+"F4.wireOp",EDGE,"E25.31.4"),sQuery(id+"F4.wireOp",EDGE,"E25.31.5"),sQuery(id+"F4.wireOp",EDGE,"E25.31.6")])],"isStart":false});
            var sketch = newSketch(context, id + "F6", { "sketchPlane" : qUnion([Q0])});
            skCircle(sketch, "E26", {"center": v(0, 0) * mm, "radius": 4.75 * mm});
            skLineSegment(sketch, "E27.bottom", {"start": v(8.5, 5) * mm, "end": v(11.5, 5) * mm});
            skLineSegment(sketch, "E27.top", {"start": v(8.5, -5) * mm, "end": v(11.5, -5) * mm});
            skLineSegment(sketch, "E27.left", {"start": v(8.5, 5) * mm, "end": v(8.5, -5) * mm});
            skLineSegment(sketch, "E27.right", {"start": v(11.5, 5) * mm, "end": v(11.5, -5) * mm});
            skPoint(sketch, "E27.middle", {"position": v(10, 0) * mm});
            skLineSegment(sketch, "E28.bottom", {"start": v(-11.5, 5) * mm, "end": v(-8.5, 5) * mm});
            skLineSegment(sketch, "E28.top", {"start": v(-11.5, -5) * mm, "end": v(-8.5, -5) * mm});
            skLineSegment(sketch, "E28.left", {"start": v(-11.5, 5) * mm, "end": v(-11.5, -5) * mm});
            skLineSegment(sketch, "E28.right", {"start": v(-8.5, 5) * mm, "end": v(-8.5, -5) * mm});
            skPoint(sketch, "E28.middle", {"position": v(-10, 0) * mm});
            skSolve(sketch);
        }
        {
            var Q0;
            Q0=makeQuery(id+"F6.imprint","IMPRINT",FACE,{"disambiguationData":[TD([[makeQuery(id+"F6.imprint","IMPRINT",EDGE,{"derivedFrom":sQuery(id+"F6.wireOp",EDGE,"E26")}),1.0]])]});
            var Q1;
            Q1=makeQuery(id+"F6.imprint","IMPRINT",FACE,{"disambiguationData":[TD([[makeQuery(id+"F6.imprint","IMPRINT",EDGE,{"derivedFrom":sQuery(id+"F6.wireOp",EDGE,"E28.bottom")}),-1.0]])]});
            var Q2;
            Q2=makeQuery(id+"F6.imprint","IMPRINT",FACE,{"disambiguationData":[TD([[makeQuery(id+"F6.imprint","IMPRINT",EDGE,{"derivedFrom":sQuery(id+"F6.wireOp",EDGE,"E27.bottom")}),-1.0]])]});
            extrude(context, id + "F7", {"entities" : qUnion([Q0, Q1, Q2]), "operationType" : NewBodyOperationType.REMOVE, "oppositeDirection" : true, "depth" : 25 * mm, "offsetDistance" : 25 * mm});
        }
        {
            var Q0;
            Q0 = qSketchRegion(id + "F4", true);
            extrude(context, id + "F8", {"entities" : qUnion([Q0]), "depth" : 3 * mm, "offsetDistance" : 25 * mm});
        }
        {
            var Q0;
            Q0=makeQuery(id+"F5.opExtrude","CAP_FACE",FACE,{"disambiguationData":[OSD([sQuery(id+"F4.wireOp",EDGE,"E18.0"),sQuery(id+"F4.wireOp",EDGE,"E19.0"),sQuery(id+"F4.wireOp",EDGE,"E20.0"),sQuery(id+"F4.wireOp",EDGE,"E21.0"),sQuery(id+"F4.wireOp",EDGE,"E23"),sQuery(id+"F4.wireOp",EDGE,"E24"),sQuery(id+"F4.wireOp",EDGE,"E25.1.0"),sQuery(id+"F4.wireOp",EDGE,"E25.1.1"),sQuery(id+"F4.wireOp",EDGE,"E25.1.3"),sQuery(id+"F4.wireOp",EDGE,"E25.1.4"),sQuery(id+"F4.wireOp",EDGE,"E25.1.5"),sQuery(id+"F4.wireOp",EDGE,"E25.1.6"),sQuery(id+"F4.wireOp",EDGE,"E25.2.0"),sQuery(id+"F4.wireOp",EDGE,"E25.2.1"),sQuery(id+"F4.wireOp",EDGE,"E25.2.3"),sQuery(id+"F4.wireOp",EDGE,"E25.2.4"),sQuery(id+"F4.wireOp",EDGE,"E25.2.5"),sQuery(id+"F4.wireOp",EDGE,"E25.2.6"),sQuery(id+"F4.wireOp",EDGE,"E25.3.0"),sQuery(id+"F4.wireOp",EDGE,"E25.3.1"),sQuery(id+"F4.wireOp",EDGE,"E25.3.3"),sQuery(id+"F4.wireOp",EDGE,"E25.3.4"),sQuery(id+"F4.wireOp",EDGE,"E25.3.5"),sQuery(id+"F4.wireOp",EDGE,"E25.3.6"),sQuery(id+"F4.wireOp",EDGE,"E25.4.0"),sQuery(id+"F4.wireOp",EDGE,"E25.4.1"),sQuery(id+"F4.wireOp",EDGE,"E25.4.3"),sQuery(id+"F4.wireOp",EDGE,"E25.4.4"),sQuery(id+"F4.wireOp",EDGE,"E25.4.5"),sQuery(id+"F4.wireOp",EDGE,"E25.4.6"),sQuery(id+"F4.wireOp",EDGE,"E25.5.0"),sQuery(id+"F4.wireOp",EDGE,"E25.5.1"),sQuery(id+"F4.wireOp",EDGE,"E25.5.3"),sQuery(id+"F4.wireOp",EDGE,"E25.5.4"),sQuery(id+"F4.wireOp",EDGE,"E25.5.5"),sQuery(id+"F4.wireOp",EDGE,"E25.5.6"),sQuery(id+"F4.wireOp",EDGE,"E25.6.0"),sQuery(id+"F4.wireOp",EDGE,"E25.6.1"),sQuery(id+"F4.wireOp",EDGE,"E25.6.3"),sQuery(id+"F4.wireOp",EDGE,"E25.6.4"),sQuery(id+"F4.wireOp",EDGE,"E25.6.5"),sQuery(id+"F4.wireOp",EDGE,"E25.6.6"),sQuery(id+"F4.wireOp",EDGE,"E25.7.0"),sQuery(id+"F4.wireOp",EDGE,"E25.7.1"),sQuery(id+"F4.wireOp",EDGE,"E25.7.3"),sQuery(id+"F4.wireOp",EDGE,"E25.7.4"),sQuery(id+"F4.wireOp",EDGE,"E25.7.5"),sQuery(id+"F4.wireOp",EDGE,"E25.7.6"),sQuery(id+"F4.wireOp",EDGE,"E25.8.0"),sQuery(id+"F4.wireOp",EDGE,"E25.8.1"),sQuery(id+"F4.wireOp",EDGE,"E25.8.3"),sQuery(id+"F4.wireOp",EDGE,"E25.8.4"),sQuery(id+"F4.wireOp",EDGE,"E25.8.5"),sQuery(id+"F4.wireOp",EDGE,"E25.8.6"),sQuery(id+"F4.wireOp",EDGE,"E25.9.0"),sQuery(id+"F4.wireOp",EDGE,"E25.9.1"),sQuery(id+"F4.wireOp",EDGE,"E25.9.3"),sQuery(id+"F4.wireOp",EDGE,"E25.9.4"),sQuery(id+"F4.wireOp",EDGE,"E25.9.5"),sQuery(id+"F4.wireOp",EDGE,"E25.9.6"),sQuery(id+"F4.wireOp",EDGE,"E25.10.0"),sQuery(id+"F4.wireOp",EDGE,"E25.10.1"),sQuery(id+"F4.wireOp",EDGE,"E25.10.3"),sQuery(id+"F4.wireOp",EDGE,"E25.10.4"),sQuery(id+"F4.wireOp",EDGE,"E25.10.5"),sQuery(id+"F4.wireOp",EDGE,"E25.10.6"),sQuery(id+"F4.wireOp",EDGE,"E25.11.0"),sQuery(id+"F4.wireOp",EDGE,"E25.11.1"),sQuery(id+"F4.wireOp",EDGE,"E25.11.3"),sQuery(id+"F4.wireOp",EDGE,"E25.11.4"),sQuery(id+"F4.wireOp",EDGE,"E25.11.5"),sQuery(id+"F4.wireOp",EDGE,"E25.11.6"),sQuery(id+"F4.wireOp",EDGE,"E25.12.0"),sQuery(id+"F4.wireOp",EDGE,"E25.12.1"),sQuery(id+"F4.wireOp",EDGE,"E25.12.3"),sQuery(id+"F4.wireOp",EDGE,"E25.12.4"),sQuery(id+"F4.wireOp",EDGE,"E25.12.5"),sQuery(id+"F4.wireOp",EDGE,"E25.12.6"),sQuery(id+"F4.wireOp",EDGE,"E25.13.0"),sQuery(id+"F4.wireOp",EDGE,"E25.13.1"),sQuery(id+"F4.wireOp",EDGE,"E25.13.3"),sQuery(id+"F4.wireOp",EDGE,"E25.13.4"),sQuery(id+"F4.wireOp",EDGE,"E25.13.5"),sQuery(id+"F4.wireOp",EDGE,"E25.13.6"),sQuery(id+"F4.wireOp",EDGE,"E25.14.0"),sQuery(id+"F4.wireOp",EDGE,"E25.14.1"),sQuery(id+"F4.wireOp",EDGE,"E25.14.3"),sQuery(id+"F4.wireOp",EDGE,"E25.14.4"),sQuery(id+"F4.wireOp",EDGE,"E25.14.5"),sQuery(id+"F4.wireOp",EDGE,"E25.14.6"),sQuery(id+"F4.wireOp",EDGE,"E25.15.0"),sQuery(id+"F4.wireOp",EDGE,"E25.15.1"),sQuery(id+"F4.wireOp",EDGE,"E25.15.3"),sQuery(id+"F4.wireOp",EDGE,"E25.15.4"),sQuery(id+"F4.wireOp",EDGE,"E25.15.5"),sQuery(id+"F4.wireOp",EDGE,"E25.15.6"),sQuery(id+"F4.wireOp",EDGE,"E25.16.0"),sQuery(id+"F4.wireOp",EDGE,"E25.16.1"),sQuery(id+"F4.wireOp",EDGE,"E25.16.3"),sQuery(id+"F4.wireOp",EDGE,"E25.16.4"),sQuery(id+"F4.wireOp",EDGE,"E25.16.5"),sQuery(id+"F4.wireOp",EDGE,"E25.16.6"),sQuery(id+"F4.wireOp",EDGE,"E25.17.0"),sQuery(id+"F4.wireOp",EDGE,"E25.17.1"),sQuery(id+"F4.wireOp",EDGE,"E25.17.3"),sQuery(id+"F4.wireOp",EDGE,"E25.17.4"),sQuery(id+"F4.wireOp",EDGE,"E25.17.5"),sQuery(id+"F4.wireOp",EDGE,"E25.17.6"),sQuery(id+"F4.wireOp",EDGE,"E25.18.0"),sQuery(id+"F4.wireOp",EDGE,"E25.18.1"),sQuery(id+"F4.wireOp",EDGE,"E25.18.3"),sQuery(id+"F4.wireOp",EDGE,"E25.18.4"),sQuery(id+"F4.wireOp",EDGE,"E25.18.5"),sQuery(id+"F4.wireOp",EDGE,"E25.18.6"),sQuery(id+"F4.wireOp",EDGE,"E25.19.0"),sQuery(id+"F4.wireOp",EDGE,"E25.19.1"),sQuery(id+"F4.wireOp",EDGE,"E25.19.3"),sQuery(id+"F4.wireOp",EDGE,"E25.19.4"),sQuery(id+"F4.wireOp",EDGE,"E25.19.5"),sQuery(id+"F4.wireOp",EDGE,"E25.19.6"),sQuery(id+"F4.wireOp",EDGE,"E25.20.0"),sQuery(id+"F4.wireOp",EDGE,"E25.20.1"),sQuery(id+"F4.wireOp",EDGE,"E25.20.3"),sQuery(id+"F4.wireOp",EDGE,"E25.20.4"),sQuery(id+"F4.wireOp",EDGE,"E25.20.5"),sQuery(id+"F4.wireOp",EDGE,"E25.20.6"),sQuery(id+"F4.wireOp",EDGE,"E25.21.0"),sQuery(id+"F4.wireOp",EDGE,"E25.21.1"),sQuery(id+"F4.wireOp",EDGE,"E25.21.3"),sQuery(id+"F4.wireOp",EDGE,"E25.21.4"),sQuery(id+"F4.wireOp",EDGE,"E25.21.5"),sQuery(id+"F4.wireOp",EDGE,"E25.21.6"),sQuery(id+"F4.wireOp",EDGE,"E25.22.0"),sQuery(id+"F4.wireOp",EDGE,"E25.22.1"),sQuery(id+"F4.wireOp",EDGE,"E25.22.3"),sQuery(id+"F4.wireOp",EDGE,"E25.22.4"),sQuery(id+"F4.wireOp",EDGE,"E25.22.5"),sQuery(id+"F4.wireOp",EDGE,"E25.22.6"),sQuery(id+"F4.wireOp",EDGE,"E25.23.0"),sQuery(id+"F4.wireOp",EDGE,"E25.23.1"),sQuery(id+"F4.wireOp",EDGE,"E25.23.3"),sQuery(id+"F4.wireOp",EDGE,"E25.23.4"),sQuery(id+"F4.wireOp",EDGE,"E25.23.5"),sQuery(id+"F4.wireOp",EDGE,"E25.23.6"),sQuery(id+"F4.wireOp",EDGE,"E25.24.0"),sQuery(id+"F4.wireOp",EDGE,"E25.24.1"),sQuery(id+"F4.wireOp",EDGE,"E25.24.3"),sQuery(id+"F4.wireOp",EDGE,"E25.24.4"),sQuery(id+"F4.wireOp",EDGE,"E25.24.5"),sQuery(id+"F4.wireOp",EDGE,"E25.24.6"),sQuery(id+"F4.wireOp",EDGE,"E25.25.0"),sQuery(id+"F4.wireOp",EDGE,"E25.25.1"),sQuery(id+"F4.wireOp",EDGE,"E25.25.3"),sQuery(id+"F4.wireOp",EDGE,"E25.25.4"),sQuery(id+"F4.wireOp",EDGE,"E25.25.5"),sQuery(id+"F4.wireOp",EDGE,"E25.25.6"),sQuery(id+"F4.wireOp",EDGE,"E25.26.0"),sQuery(id+"F4.wireOp",EDGE,"E25.26.1"),sQuery(id+"F4.wireOp",EDGE,"E25.26.3"),sQuery(id+"F4.wireOp",EDGE,"E25.26.4"),sQuery(id+"F4.wireOp",EDGE,"E25.26.5"),sQuery(id+"F4.wireOp",EDGE,"E25.26.6"),sQuery(id+"F4.wireOp",EDGE,"E25.27.0"),sQuery(id+"F4.wireOp",EDGE,"E25.27.1"),sQuery(id+"F4.wireOp",EDGE,"E25.27.3"),sQuery(id+"F4.wireOp",EDGE,"E25.27.4"),sQuery(id+"F4.wireOp",EDGE,"E25.27.5"),sQuery(id+"F4.wireOp",EDGE,"E25.27.6"),sQuery(id+"F4.wireOp",EDGE,"E25.28.0"),sQuery(id+"F4.wireOp",EDGE,"E25.28.1"),sQuery(id+"F4.wireOp",EDGE,"E25.28.3"),sQuery(id+"F4.wireOp",EDGE,"E25.28.4"),sQuery(id+"F4.wireOp",EDGE,"E25.28.5"),sQuery(id+"F4.wireOp",EDGE,"E25.28.6"),sQuery(id+"F4.wireOp",EDGE,"E25.29.0"),sQuery(id+"F4.wireOp",EDGE,"E25.29.1"),sQuery(id+"F4.wireOp",EDGE,"E25.29.3"),sQuery(id+"F4.wireOp",EDGE,"E25.29.4"),sQuery(id+"F4.wireOp",EDGE,"E25.29.5"),sQuery(id+"F4.wireOp",EDGE,"E25.29.6"),sQuery(id+"F4.wireOp",EDGE,"E25.30.0"),sQuery(id+"F4.wireOp",EDGE,"E25.30.1"),sQuery(id+"F4.wireOp",EDGE,"E25.30.3"),sQuery(id+"F4.wireOp",EDGE,"E25.30.4"),sQuery(id+"F4.wireOp",EDGE,"E25.30.5"),sQuery(id+"F4.wireOp",EDGE,"E25.30.6"),sQuery(id+"F4.wireOp",EDGE,"E25.31.0"),sQuery(id+"F4.wireOp",EDGE,"E25.31.1"),sQuery(id+"F4.wireOp",EDGE,"E25.31.3"),sQuery(id+"F4.wireOp",EDGE,"E25.31.4"),sQuery(id+"F4.wireOp",EDGE,"E25.31.5"),sQuery(id+"F4.wireOp",EDGE,"E25.31.6")])],"isStart":false});
            var sketch = newSketch(context, id + "F9", { "sketchPlane" : qUnion([Q0])});
            skLineSegment(sketch, "E29.bottom", {"start": v(4.5, 1.5) * mm, "end": v(-4.5, 1.5) * mm});
            skLineSegment(sketch, "E29.top", {"start": v(4.5, -1.5) * mm, "end": v(-4.5, -1.5) * mm});
            skLineSegment(sketch, "E29.left", {"start": v(4.5, 1.5) * mm, "end": v(4.5, -1.5) * mm});
            skLineSegment(sketch, "E29.right", {"start": v(-4.5, 1.5) * mm, "end": v(-4.5, -1.5) * mm});
            skPoint(sketch, "E29.middle", {"position": v(0, 0) * mm});
            skLineSegment(sketch, "E30.bottom", {"start": v(1.5, 4.5) * mm, "end": v(-1.5, 4.5) * mm});
            skLineSegment(sketch, "E30.top", {"start": v(1.5, -4.5) * mm, "end": v(-1.5, -4.5) * mm});
            skLineSegment(sketch, "E30.left", {"start": v(1.5, 4.5) * mm, "end": v(1.5, -4.5) * mm});
            skLineSegment(sketch, "E30.right", {"start": v(-1.5, 4.5) * mm, "end": v(-1.5, -4.5) * mm});
            skSolve(sketch);
        }
        {
            var Q0;
            Q0 = qSketchRegion(id + "F9", true);
            extrude(context, id + "F10", {"entities" : qUnion([Q0]), "operationType" : NewBodyOperationType.REMOVE, "oppositeDirection" : true, "depth" : 25 * mm, "offsetDistance" : 25 * mm});
        }
        {
            var Q0;
            Q0=qCreatedBy(makeId("Front.planeOp"),FACE);
            var sketch = newSketch(context, id + "F11", { "sketchPlane" : qUnion([Q0])});
            skArc(sketch, "E31.0", {"start": v(-64.1, 62.6) * mm, "mid": v(-64.78, 62.75) * mm, "end": v(-65.46, 62.88) * mm});
            skArc(sketch, "E32.0", {"start": v(-63.46, 57.52) * mm, "mid": v(-63.88, 57.9) * mm, "end": v(-63.92, 58.48) * mm});
            skArc(sketch, "E33.0", {"start": v(-62.66, 57.19) * mm, "mid": v(-63.06, 57.36) * mm, "end": v(-63.46, 57.52) * mm});
            skArc(sketch, "E34.0", {"start": v(-61.65, 57.54) * mm, "mid": v(-62.08, 57.16) * mm, "end": v(-62.66, 57.19) * mm});
            skPoint(sketch, "E35.0", {"position": v(-58.6, 60.33) * mm});
            skArc(sketch, "E36", {"start": v(-63.92, 58.48) * mm, "mid": v(-63.64, 60.56) * mm, "end": v(-64.1, 62.6) * mm});
            skArc(sketch, "E37", {"start": v(-61.65, 57.54) * mm, "mid": v(-60.38, 59.2) * mm, "end": v(-58.6, 60.33) * mm});
            skArc(sketch, "E38.1.0", {"start": v(-57.12, 53.94) * mm, "mid": v(-57.67, 53.76) * mm, "end": v(-58.2, 54) * mm});
            skArc(sketch, "E38.1.1", {"start": v(-58.2, 54) * mm, "mid": v(-58.5, 54.3) * mm, "end": v(-58.8, 54.6) * mm});
            skArc(sketch, "E38.1.2", {"start": v(-58.86, 55.68) * mm, "mid": v(-57.8, 57.5) * mm, "end": v(-57.45, 59.56) * mm});
            skArc(sketch, "E38.1.3", {"start": v(-57.12, 53.94) * mm, "mid": v(-55.3, 55) * mm, "end": v(-53.24, 55.35) * mm});
            skArc(sketch, "E38.1.4", {"start": v(-57.45, 59.56) * mm, "mid": v(-58.02, 59.96) * mm, "end": v(-58.6, 60.33) * mm});
            skArc(sketch, "E38.1.5", {"start": v(-58.8, 54.6) * mm, "mid": v(-59.05, 55.13) * mm, "end": v(-58.86, 55.68) * mm});
            skPoint(sketch, "E38.1.6", {"position": v(-53.24, 55.35) * mm});
            skArc(sketch, "E38.2.0", {"start": v(-54.32, 48.88) * mm, "mid": v(-54.9, 48.92) * mm, "end": v(-55.29, 49.35) * mm});
            skArc(sketch, "E38.2.1", {"start": v(-55.29, 49.35) * mm, "mid": v(-55.45, 49.75) * mm, "end": v(-55.62, 50.14) * mm});
            skArc(sketch, "E38.2.2", {"start": v(-55.26, 51.16) * mm, "mid": v(-53.6, 52.43) * mm, "end": v(-52.47, 54.2) * mm});
            skArc(sketch, "E38.2.3", {"start": v(-54.32, 48.88) * mm, "mid": v(-52.24, 49.16) * mm, "end": v(-50.2, 48.7) * mm});
            skArc(sketch, "E38.2.4", {"start": v(-52.47, 54.2) * mm, "mid": v(-52.85, 54.78) * mm, "end": v(-53.24, 55.35) * mm});
            skArc(sketch, "E38.2.5", {"start": v(-55.62, 50.14) * mm, "mid": v(-55.64, 50.72) * mm, "end": v(-55.26, 51.16) * mm});
            skPoint(sketch, "E38.2.6", {"position": v(-50.2, 48.7) * mm});
            skArc(sketch, "E38.3.0", {"start": v(-53.67, 43.14) * mm, "mid": v(-54.18, 43.4) * mm, "end": v(-54.38, 43.94) * mm});
            skArc(sketch, "E38.3.1", {"start": v(-54.38, 43.94) * mm, "mid": v(-54.38, 44.37) * mm, "end": v(-54.38, 44.8) * mm});
            skArc(sketch, "E38.3.2", {"start": v(-53.67, 45.6) * mm, "mid": v(-51.64, 46.13) * mm, "end": v(-49.93, 47.34) * mm});
            skArc(sketch, "E38.3.3", {"start": v(-53.67, 43.14) * mm, "mid": v(-51.64, 42.6) * mm, "end": v(-49.93, 41.4) * mm});
            skArc(sketch, "E38.3.4", {"start": v(-49.93, 47.34) * mm, "mid": v(-50.05, 48.02) * mm, "end": v(-50.2, 48.7) * mm});
            skArc(sketch, "E38.3.5", {"start": v(-54.38, 44.8) * mm, "mid": v(-54.18, 45.34) * mm, "end": v(-53.67, 45.6) * mm});
            skPoint(sketch, "E38.3.6", {"position": v(-49.93, 41.4) * mm});
            skArc(sketch, "E38.4.0", {"start": v(-55.26, 37.58) * mm, "mid": v(-55.64, 38.01) * mm, "end": v(-55.62, 38.6) * mm});
            skArc(sketch, "E38.4.1", {"start": v(-55.62, 38.6) * mm, "mid": v(-55.45, 38.99) * mm, "end": v(-55.29, 39.39) * mm});
            skArc(sketch, "E38.4.2", {"start": v(-54.32, 39.85) * mm, "mid": v(-52.24, 39.57) * mm, "end": v(-50.2, 40.03) * mm});
            skArc(sketch, "E38.4.3", {"start": v(-55.26, 37.58) * mm, "mid": v(-53.6, 36.3) * mm, "end": v(-52.47, 34.53) * mm});
            skArc(sketch, "E38.4.4", {"start": v(-50.2, 40.03) * mm, "mid": v(-50.05, 40.7) * mm, "end": v(-49.93, 41.4) * mm});
            skArc(sketch, "E38.4.5", {"start": v(-55.29, 39.39) * mm, "mid": v(-54.9, 39.81) * mm, "end": v(-54.32, 39.85) * mm});
            skPoint(sketch, "E38.4.6", {"position": v(-52.47, 34.53) * mm});
            skArc(sketch, "E38.5.0", {"start": v(-58.86, 33.05) * mm, "mid": v(-59.05, 33.6) * mm, "end": v(-58.8, 34.13) * mm});
            skArc(sketch, "E38.5.1", {"start": v(-58.8, 34.13) * mm, "mid": v(-58.5, 34.42) * mm, "end": v(-58.2, 34.73) * mm});
            skArc(sketch, "E38.5.2", {"start": v(-57.12, 34.8) * mm, "mid": v(-55.3, 33.74) * mm, "end": v(-53.24, 33.38) * mm});
            skArc(sketch, "E38.5.3", {"start": v(-58.86, 33.05) * mm, "mid": v(-57.8, 31.24) * mm, "end": v(-57.45, 29.17) * mm});
            skArc(sketch, "E38.5.4", {"start": v(-53.24, 33.38) * mm, "mid": v(-52.85, 33.95) * mm, "end": v(-52.47, 34.53) * mm});
            skArc(sketch, "E38.5.5", {"start": v(-58.2, 34.73) * mm, "mid": v(-57.67, 34.98) * mm, "end": v(-57.12, 34.8) * mm});
            skPoint(sketch, "E38.5.6", {"position": v(-57.45, 29.17) * mm});
            skArc(sketch, "E38.6.0", {"start": v(-63.92, 30.25) * mm, "mid": v(-63.88, 30.83) * mm, "end": v(-63.46, 31.22) * mm});
            skArc(sketch, "E38.6.1", {"start": v(-63.46, 31.22) * mm, "mid": v(-63.06, 31.38) * mm, "end": v(-62.66, 31.55) * mm});
            skArc(sketch, "E38.6.2", {"start": v(-61.65, 31.2) * mm, "mid": v(-60.38, 29.52) * mm, "end": v(-58.6, 28.4) * mm});
            skArc(sketch, "E38.6.3", {"start": v(-63.92, 30.25) * mm, "mid": v(-63.64, 28.17) * mm, "end": v(-64.1, 26.13) * mm});
            skArc(sketch, "E38.6.4", {"start": v(-58.6, 28.4) * mm, "mid": v(-58.02, 28.78) * mm, "end": v(-57.45, 29.17) * mm});
            skArc(sketch, "E38.6.5", {"start": v(-62.66, 31.55) * mm, "mid": v(-62.08, 31.57) * mm, "end": v(-61.65, 31.2) * mm});
            skPoint(sketch, "E38.6.6", {"position": v(-64.1, 26.13) * mm});
            skArc(sketch, "E38.7.0", {"start": v(-69.67, 29.6) * mm, "mid": v(-69.41, 30.11) * mm, "end": v(-68.87, 30.31) * mm});
            skArc(sketch, "E38.7.1", {"start": v(-68.87, 30.31) * mm, "mid": v(-68.44, 30.3) * mm, "end": v(-68, 30.31) * mm});
            skArc(sketch, "E38.7.2", {"start": v(-67.2, 29.6) * mm, "mid": v(-66.67, 27.57) * mm, "end": v(-65.46, 25.86) * mm});
            skArc(sketch, "E38.7.3", {"start": v(-69.67, 29.6) * mm, "mid": v(-70.2, 27.57) * mm, "end": v(-71.41, 25.86) * mm});
            skArc(sketch, "E38.7.4", {"start": v(-65.46, 25.86) * mm, "mid": v(-64.78, 25.98) * mm, "end": v(-64.1, 26.13) * mm});
            skArc(sketch, "E38.7.5", {"start": v(-68, 30.31) * mm, "mid": v(-67.46, 30.11) * mm, "end": v(-67.2, 29.6) * mm});
            skPoint(sketch, "E38.7.6", {"position": v(-71.41, 25.86) * mm});
            skArc(sketch, "E38.8.0", {"start": v(-75.23, 31.2) * mm, "mid": v(-74.8, 31.57) * mm, "end": v(-74.21, 31.55) * mm});
            skArc(sketch, "E38.8.1", {"start": v(-74.21, 31.55) * mm, "mid": v(-73.82, 31.38) * mm, "end": v(-73.42, 31.22) * mm});
            skArc(sketch, "E38.8.2", {"start": v(-72.95, 30.25) * mm, "mid": v(-73.23, 28.17) * mm, "end": v(-72.77, 26.13) * mm});
            skArc(sketch, "E38.8.3", {"start": v(-75.23, 31.2) * mm, "mid": v(-76.5, 29.52) * mm, "end": v(-78.27, 28.4) * mm});
            skArc(sketch, "E38.8.4", {"start": v(-72.77, 26.13) * mm, "mid": v(-72.1, 25.98) * mm, "end": v(-71.41, 25.86) * mm});
            skArc(sketch, "E38.8.5", {"start": v(-73.42, 31.22) * mm, "mid": v(-73, 30.83) * mm, "end": v(-72.95, 30.25) * mm});
            skPoint(sketch, "E38.8.6", {"position": v(-78.27, 28.4) * mm});
            skArc(sketch, "E38.9.0", {"start": v(-79.75, 34.8) * mm, "mid": v(-79.2, 34.98) * mm, "end": v(-78.68, 34.73) * mm});
            skArc(sketch, "E38.9.1", {"start": v(-78.68, 34.73) * mm, "mid": v(-78.38, 34.42) * mm, "end": v(-78.07, 34.13) * mm});
            skArc(sketch, "E38.9.2", {"start": v(-78.01, 33.05) * mm, "mid": v(-79.06, 31.24) * mm, "end": v(-79.42, 29.17) * mm});
            skArc(sketch, "E38.9.3", {"start": v(-79.75, 34.8) * mm, "mid": v(-81.56, 33.74) * mm, "end": v(-83.63, 33.38) * mm});
            skArc(sketch, "E38.9.4", {"start": v(-79.42, 29.17) * mm, "mid": v(-78.85, 28.78) * mm, "end": v(-78.27, 28.4) * mm});
            skArc(sketch, "E38.9.5", {"start": v(-78.07, 34.13) * mm, "mid": v(-77.83, 33.6) * mm, "end": v(-78.01, 33.05) * mm});
            skPoint(sketch, "E38.9.6", {"position": v(-83.63, 33.38) * mm});
            skArc(sketch, "E38.10.0", {"start": v(-82.55, 39.85) * mm, "mid": v(-81.98, 39.81) * mm, "end": v(-81.59, 39.39) * mm});
            skArc(sketch, "E38.10.1", {"start": v(-81.59, 39.39) * mm, "mid": v(-81.43, 38.99) * mm, "end": v(-81.26, 38.6) * mm});
            skArc(sketch, "E38.10.2", {"start": v(-81.61, 37.58) * mm, "mid": v(-83.28, 36.3) * mm, "end": v(-84.4, 34.53) * mm});
            skArc(sketch, "E38.10.3", {"start": v(-82.55, 39.85) * mm, "mid": v(-84.63, 39.57) * mm, "end": v(-86.68, 40.03) * mm});
            skArc(sketch, "E38.10.4", {"start": v(-84.4, 34.53) * mm, "mid": v(-84.03, 33.95) * mm, "end": v(-83.63, 33.38) * mm});
            skArc(sketch, "E38.10.5", {"start": v(-81.26, 38.6) * mm, "mid": v(-81.23, 38.01) * mm, "end": v(-81.61, 37.58) * mm});
            skPoint(sketch, "E38.10.6", {"position": v(-86.68, 40.03) * mm});
            skArc(sketch, "E38.11.0", {"start": v(-83.2, 45.6) * mm, "mid": v(-82.69, 45.34) * mm, "end": v(-82.5, 44.8) * mm});
            skArc(sketch, "E38.11.1", {"start": v(-82.5, 44.8) * mm, "mid": v(-82.5, 44.37) * mm, "end": v(-82.5, 43.94) * mm});
            skArc(sketch, "E38.11.2", {"start": v(-83.2, 43.14) * mm, "mid": v(-85.23, 42.6) * mm, "end": v(-86.95, 41.4) * mm});
            skArc(sketch, "E38.11.3", {"start": v(-83.2, 45.6) * mm, "mid": v(-85.23, 46.13) * mm, "end": v(-86.95, 47.34) * mm});
            skArc(sketch, "E38.11.4", {"start": v(-86.95, 41.4) * mm, "mid": v(-86.82, 40.7) * mm, "end": v(-86.68, 40.03) * mm});
            skArc(sketch, "E38.11.5", {"start": v(-82.5, 43.94) * mm, "mid": v(-82.69, 43.4) * mm, "end": v(-83.2, 43.14) * mm});
            skPoint(sketch, "E38.11.6", {"position": v(-86.95, 47.34) * mm});
            skArc(sketch, "E38.12.0", {"start": v(-81.61, 51.16) * mm, "mid": v(-81.23, 50.72) * mm, "end": v(-81.26, 50.14) * mm});
            skArc(sketch, "E38.12.1", {"start": v(-81.26, 50.14) * mm, "mid": v(-81.43, 49.75) * mm, "end": v(-81.59, 49.35) * mm});
            skArc(sketch, "E38.12.2", {"start": v(-82.55, 48.88) * mm, "mid": v(-84.63, 49.16) * mm, "end": v(-86.68, 48.7) * mm});
            skArc(sketch, "E38.12.3", {"start": v(-81.61, 51.16) * mm, "mid": v(-83.28, 52.43) * mm, "end": v(-84.4, 54.2) * mm});
            skArc(sketch, "E38.12.4", {"start": v(-86.68, 48.7) * mm, "mid": v(-86.82, 48.02) * mm, "end": v(-86.95, 47.34) * mm});
            skArc(sketch, "E38.12.5", {"start": v(-81.59, 49.35) * mm, "mid": v(-81.98, 48.92) * mm, "end": v(-82.55, 48.88) * mm});
            skPoint(sketch, "E38.12.6", {"position": v(-84.4, 54.2) * mm});
            skArc(sketch, "E38.13.0", {"start": v(-78.01, 55.68) * mm, "mid": v(-77.83, 55.13) * mm, "end": v(-78.07, 54.6) * mm});
            skArc(sketch, "E38.13.1", {"start": v(-78.07, 54.6) * mm, "mid": v(-78.38, 54.3) * mm, "end": v(-78.68, 54) * mm});
            skArc(sketch, "E38.13.2", {"start": v(-79.75, 53.94) * mm, "mid": v(-81.56, 55) * mm, "end": v(-83.63, 55.35) * mm});
            skArc(sketch, "E38.13.3", {"start": v(-78.01, 55.68) * mm, "mid": v(-79.06, 57.5) * mm, "end": v(-79.42, 59.56) * mm});
            skArc(sketch, "E38.13.4", {"start": v(-83.63, 55.35) * mm, "mid": v(-84.03, 54.78) * mm, "end": v(-84.4, 54.2) * mm});
            skArc(sketch, "E38.13.5", {"start": v(-78.68, 54) * mm, "mid": v(-79.2, 53.76) * mm, "end": v(-79.75, 53.94) * mm});
            skPoint(sketch, "E38.13.6", {"position": v(-79.42, 59.56) * mm});
            skArc(sketch, "E38.14.0", {"start": v(-72.95, 58.48) * mm, "mid": v(-73, 57.9) * mm, "end": v(-73.42, 57.52) * mm});
            skArc(sketch, "E38.14.1", {"start": v(-73.42, 57.52) * mm, "mid": v(-73.82, 57.36) * mm, "end": v(-74.21, 57.19) * mm});
            skArc(sketch, "E38.14.2", {"start": v(-75.23, 57.54) * mm, "mid": v(-76.5, 59.2) * mm, "end": v(-78.27, 60.33) * mm});
            skArc(sketch, "E38.14.3", {"start": v(-72.95, 58.48) * mm, "mid": v(-73.23, 60.56) * mm, "end": v(-72.77, 62.6) * mm});
            skArc(sketch, "E38.14.4", {"start": v(-78.27, 60.33) * mm, "mid": v(-78.85, 59.96) * mm, "end": v(-79.42, 59.56) * mm});
            skArc(sketch, "E38.14.5", {"start": v(-74.21, 57.19) * mm, "mid": v(-74.8, 57.16) * mm, "end": v(-75.23, 57.54) * mm});
            skPoint(sketch, "E38.14.6", {"position": v(-72.77, 62.6) * mm});
            skArc(sketch, "E38.15.0", {"start": v(-67.2, 59.14) * mm, "mid": v(-67.46, 58.62) * mm, "end": v(-68, 58.42) * mm});
            skArc(sketch, "E38.15.1", {"start": v(-68, 58.42) * mm, "mid": v(-68.44, 58.43) * mm, "end": v(-68.87, 58.42) * mm});
            skArc(sketch, "E38.15.2", {"start": v(-69.67, 59.14) * mm, "mid": v(-70.2, 61.16) * mm, "end": v(-71.41, 62.88) * mm});
            skArc(sketch, "E38.15.3", {"start": v(-67.2, 59.14) * mm, "mid": v(-66.67, 61.16) * mm, "end": v(-65.46, 62.88) * mm});
            skArc(sketch, "E38.15.4", {"start": v(-71.41, 62.88) * mm, "mid": v(-72.1, 62.75) * mm, "end": v(-72.77, 62.6) * mm});
            skArc(sketch, "E38.15.5", {"start": v(-68.87, 58.42) * mm, "mid": v(-69.41, 58.62) * mm, "end": v(-69.67, 59.14) * mm});
            skPoint(sketch, "E38.15.6", {"position": v(-65.46, 62.88) * mm});
            skLineSegment(sketch, "E38.anchor1", {"start": v(-68.44, 44.37) * mm, "end": v(-69.56, 60.3) * mm, "construction": true});
            skLineSegment(sketch, "E38.anchor2", {"start": v(-68.44, 44.37) * mm, "end": v(-75.58, 58.66) * mm, "construction": true});
            skLineSegment(sketch, "E39.bottom", {"start": v(-67.06, 45.74) * mm, "end": v(-69.81, 45.74) * mm});
            skLineSegment(sketch, "E39.top", {"start": v(-67.06, 43) * mm, "end": v(-69.81, 43) * mm});
            skLineSegment(sketch, "E39.left", {"start": v(-67.06, 45.74) * mm, "end": v(-67.06, 43) * mm});
            skLineSegment(sketch, "E39.right", {"start": v(-69.81, 45.74) * mm, "end": v(-69.81, 43) * mm});
            skLineSegment(sketch, "E40", {"start": v(-68.44, 25.36) * mm, "end": v(-68.44, 61.66) * mm, "construction": true});
            skLineSegment(sketch, "E41.bottom", {"start": v(-67.06, 35.74) * mm, "end": v(-69.81, 35.74) * mm});
            skLineSegment(sketch, "E41.top", {"start": v(-67.06, 33) * mm, "end": v(-69.81, 33) * mm});
            skLineSegment(sketch, "E41.left", {"start": v(-67.06, 35.74) * mm, "end": v(-67.06, 33) * mm});
            skLineSegment(sketch, "E41.right", {"start": v(-69.81, 35.74) * mm, "end": v(-69.81, 33) * mm});
            skPoint(sketch, "E41.middle", {"position": v(-68.44, 34.37) * mm});
            skPoint(sketch, "E42.middle", {"position": v(-68.44, 54.37) * mm});
            skSolve(sketch);
        }
        {
            var Q0;
            Q0=makeQuery(id+"F11.imprint","IMPRINT",FACE,{"disambiguationData":[TD([[makeQuery(id+"F11.imprint","IMPRINT",EDGE,{"derivedFrom":sQuery(id+"F11.wireOp",EDGE,"E31.0")}),1.0]])]});
            extrude(context, id + "F12", {"entities" : qUnion([Q0]), "depth" : 3 * mm, "offsetDistance" : 25 * mm});
        }
        {
            var Q0;
            Q0=makeQuery(id+"F12.opExtrude","CAP_FACE",FACE,{"disambiguationData":[OSD([sQuery(id+"F11.wireOp",EDGE,"E31.0"),sQuery(id+"F11.wireOp",EDGE,"E32.0"),sQuery(id+"F11.wireOp",EDGE,"E33.0"),sQuery(id+"F11.wireOp",EDGE,"E34.0"),sQuery(id+"F11.wireOp",EDGE,"E36"),sQuery(id+"F11.wireOp",EDGE,"E37"),sQuery(id+"F11.wireOp",EDGE,"E38.1.0"),sQuery(id+"F11.wireOp",EDGE,"E38.1.1"),sQuery(id+"F11.wireOp",EDGE,"E38.1.2"),sQuery(id+"F11.wireOp",EDGE,"E38.1.3"),sQuery(id+"F11.wireOp",EDGE,"E38.1.4"),sQuery(id+"F11.wireOp",EDGE,"E38.1.5"),sQuery(id+"F11.wireOp",EDGE,"E38.2.0"),sQuery(id+"F11.wireOp",EDGE,"E38.2.1"),sQuery(id+"F11.wireOp",EDGE,"E38.2.2"),sQuery(id+"F11.wireOp",EDGE,"E38.2.3"),sQuery(id+"F11.wireOp",EDGE,"E38.2.4"),sQuery(id+"F11.wireOp",EDGE,"E38.2.5"),sQuery(id+"F11.wireOp",EDGE,"E38.3.0"),sQuery(id+"F11.wireOp",EDGE,"E38.3.1"),sQuery(id+"F11.wireOp",EDGE,"E38.3.2"),sQuery(id+"F11.wireOp",EDGE,"E38.3.3"),sQuery(id+"F11.wireOp",EDGE,"E38.3.4"),sQuery(id+"F11.wireOp",EDGE,"E38.3.5"),sQuery(id+"F11.wireOp",EDGE,"E38.4.0"),sQuery(id+"F11.wireOp",EDGE,"E38.4.1"),sQuery(id+"F11.wireOp",EDGE,"E38.4.2"),sQuery(id+"F11.wireOp",EDGE,"E38.4.3"),sQuery(id+"F11.wireOp",EDGE,"E38.4.4"),sQuery(id+"F11.wireOp",EDGE,"E38.4.5"),sQuery(id+"F11.wireOp",EDGE,"E38.5.0"),sQuery(id+"F11.wireOp",EDGE,"E38.5.1"),sQuery(id+"F11.wireOp",EDGE,"E38.5.2"),sQuery(id+"F11.wireOp",EDGE,"E38.5.3"),sQuery(id+"F11.wireOp",EDGE,"E38.5.4"),sQuery(id+"F11.wireOp",EDGE,"E38.5.5"),sQuery(id+"F11.wireOp",EDGE,"E38.6.0"),sQuery(id+"F11.wireOp",EDGE,"E38.6.1"),sQuery(id+"F11.wireOp",EDGE,"E38.6.2"),sQuery(id+"F11.wireOp",EDGE,"E38.6.3"),sQuery(id+"F11.wireOp",EDGE,"E38.6.4"),sQuery(id+"F11.wireOp",EDGE,"E38.6.5"),sQuery(id+"F11.wireOp",EDGE,"E38.7.0"),sQuery(id+"F11.wireOp",EDGE,"E38.7.1"),sQuery(id+"F11.wireOp",EDGE,"E38.7.2"),sQuery(id+"F11.wireOp",EDGE,"E38.7.3"),sQuery(id+"F11.wireOp",EDGE,"E38.7.4"),sQuery(id+"F11.wireOp",EDGE,"E38.7.5"),sQuery(id+"F11.wireOp",EDGE,"E38.8.0"),sQuery(id+"F11.wireOp",EDGE,"E38.8.1"),sQuery(id+"F11.wireOp",EDGE,"E38.8.2"),sQuery(id+"F11.wireOp",EDGE,"E38.8.3"),sQuery(id+"F11.wireOp",EDGE,"E38.8.4"),sQuery(id+"F11.wireOp",EDGE,"E38.8.5"),sQuery(id+"F11.wireOp",EDGE,"E38.9.0"),sQuery(id+"F11.wireOp",EDGE,"E38.9.1"),sQuery(id+"F11.wireOp",EDGE,"E38.9.2"),sQuery(id+"F11.wireOp",EDGE,"E38.9.3"),sQuery(id+"F11.wireOp",EDGE,"E38.9.4"),sQuery(id+"F11.wireOp",EDGE,"E38.9.5"),sQuery(id+"F11.wireOp",EDGE,"E38.10.0"),sQuery(id+"F11.wireOp",EDGE,"E38.10.1"),sQuery(id+"F11.wireOp",EDGE,"E38.10.2"),sQuery(id+"F11.wireOp",EDGE,"E38.10.3"),sQuery(id+"F11.wireOp",EDGE,"E38.10.4"),sQuery(id+"F11.wireOp",EDGE,"E38.10.5"),sQuery(id+"F11.wireOp",EDGE,"E38.11.0"),sQuery(id+"F11.wireOp",EDGE,"E38.11.1"),sQuery(id+"F11.wireOp",EDGE,"E38.11.2"),sQuery(id+"F11.wireOp",EDGE,"E38.11.3"),sQuery(id+"F11.wireOp",EDGE,"E38.11.4"),sQuery(id+"F11.wireOp",EDGE,"E38.11.5"),sQuery(id+"F11.wireOp",EDGE,"E38.12.0"),sQuery(id+"F11.wireOp",EDGE,"E38.12.1"),sQuery(id+"F11.wireOp",EDGE,"E38.12.2"),sQuery(id+"F11.wireOp",EDGE,"E38.12.3"),sQuery(id+"F11.wireOp",EDGE,"E38.12.4"),sQuery(id+"F11.wireOp",EDGE,"E38.12.5"),sQuery(id+"F11.wireOp",EDGE,"E38.13.0"),sQuery(id+"F11.wireOp",EDGE,"E38.13.1"),sQuery(id+"F11.wireOp",EDGE,"E38.13.2"),sQuery(id+"F11.wireOp",EDGE,"E38.13.3"),sQuery(id+"F11.wireOp",EDGE,"E38.13.4"),sQuery(id+"F11.wireOp",EDGE,"E38.13.5"),sQuery(id+"F11.wireOp",EDGE,"E38.14.0"),sQuery(id+"F11.wireOp",EDGE,"E38.14.1"),sQuery(id+"F11.wireOp",EDGE,"E38.14.2"),sQuery(id+"F11.wireOp",EDGE,"E38.14.3"),sQuery(id+"F11.wireOp",EDGE,"E38.14.4"),sQuery(id+"F11.wireOp",EDGE,"E38.14.5"),sQuery(id+"F11.wireOp",EDGE,"E38.15.0"),sQuery(id+"F11.wireOp",EDGE,"E38.15.1"),sQuery(id+"F11.wireOp",EDGE,"E38.15.2"),sQuery(id+"F11.wireOp",EDGE,"E38.15.3"),sQuery(id+"F11.wireOp",EDGE,"E38.15.4"),sQuery(id+"F11.wireOp",EDGE,"E38.15.5"),sQuery(id+"F11.wireOp",EDGE,"E39.bottom"),sQuery(id+"F11.wireOp",EDGE,"E39.top"),sQuery(id+"F11.wireOp",EDGE,"E39.left"),sQuery(id+"F11.wireOp",EDGE,"E39.right"),sQuery(id+"F11.wireOp",EDGE,"E41.bottom"),sQuery(id+"F11.wireOp",EDGE,"E41.top"),sQuery(id+"F11.wireOp",EDGE,"E41.left"),sQuery(id+"F11.wireOp",EDGE,"E41.right")])],"isStart":false});
            var sketch = newSketch(context, id + "F13", { "sketchPlane" : qUnion([Q0])});
            skLineSegment(sketch, "E43.0", {"start": v(-67.06, 35.74) * mm, "end": v(-69.81, 35.74) * mm});
            skLineSegment(sketch, "E44", {"start": v(-69.81, 27.74) * mm, "end": v(-67.06, 27.74) * mm});
            skArc(sketch, "E45", {"start": v(-69.81, 35.74) * mm, "mid": v(-72.44, 31.74) * mm, "end": v(-69.81, 27.74) * mm});
            skArc(sketch, "E46", {"start": v(-67.06, 27.74) * mm, "mid": v(-64.44, 31.74) * mm, "end": v(-67.06, 35.74) * mm});
            skLineSegment(sketch, "E47.0", {"start": v(-69.81, 35.74) * mm, "end": v(-69.81, 33) * mm});
            skLineSegment(sketch, "E48.0", {"start": v(-67.06, 33) * mm, "end": v(-69.81, 33) * mm});
            skLineSegment(sketch, "E49.0", {"start": v(-67.06, 35.74) * mm, "end": v(-67.06, 33) * mm});
            skLineSegment(sketch, "E50", {"start": v(-72.44, 31.74) * mm, "end": v(-64.44, 31.74) * mm, "construction": true});
            skLineSegment(sketch, "E51", {"start": v(-68.44, 35.74) * mm, "end": v(-68.44, 27.74) * mm, "construction": true});
            skSolve(sketch);
        }
        {
            var Q0;
            {var subQ6=sQuery(id+"F13.wireOp",EDGE,"E47.0");Q0=makeQuery(id+"F13.imprint","IMPRINT",FACE,{"disambiguationData":[TD([[makeQuery(id+"F13.imprint","IMPRINT",EDGE,{"derivedFrom":subQ6}),-1.0]])]});}
            var Q1;
            {var subQ5=makeQuery(id+"F12.opExtrude","CAP_EDGE",EDGE,{"disambiguationData":[OSD([sQuery(id+"F11.wireOp",EDGE,"E38.6.0")])],"isStart":false});Q1=makeQuery(id+"F13.imprint","IMPRINT",FACE,{"disambiguationData":[TD([[makeQuery(id+"F13.imprint","IMPRINT",EDGE,{"derivedFrom":subQ5}),-1.0]])]});}
            var Q2;
            {var subQ5=makeQuery(id+"F12.opExtrude","CAP_EDGE",EDGE,{"disambiguationData":[OSD([sQuery(id+"F11.wireOp",EDGE,"E38.8.5")])],"isStart":false});Q2=makeQuery(id+"F13.imprint","IMPRINT",FACE,{"disambiguationData":[TD([[makeQuery(id+"F13.imprint","IMPRINT",EDGE,{"derivedFrom":subQ5}),-1.0]])]});}
            var Q3;
            {var subQ2=sQuery(id+"F13.wireOp",EDGE,"E44");Q3=makeQuery(id+"F13.imprint","IMPRINT",FACE,{"disambiguationData":[TD([[makeQuery(id+"F13.imprint","IMPRINT",EDGE,{"derivedFrom":subQ2}),1.0]])]});}
            extrude(context, id + "F14", {"entities" : qUnion([Q0, Q1, Q2, Q3]), "depth" : 3 * mm, "offsetDistance" : 25 * mm});
        }
        {
            var Q0;
            Q0=makeQuery(id+"F3.opExtrude","CAP_FACE",FACE,{"disambiguationData":[OSD([sQuery(id+"F2.wireOp",EDGE,"E9.0"),sQuery(id+"F2.wireOp",EDGE,"E10.0"),sQuery(id+"F2.wireOp",EDGE,"E11.0"),sQuery(id+"F2.wireOp",EDGE,"E12.0"),sQuery(id+"F2.wireOp",EDGE,"E14"),sQuery(id+"F2.wireOp",EDGE,"E15"),sQuery(id+"F2.wireOp",EDGE,"E16.1.0"),sQuery(id+"F2.wireOp",EDGE,"E16.1.1"),sQuery(id+"F2.wireOp",EDGE,"E16.1.2"),sQuery(id+"F2.wireOp",EDGE,"E16.1.3"),sQuery(id+"F2.wireOp",EDGE,"E16.1.4"),sQuery(id+"F2.wireOp",EDGE,"E16.1.5"),sQuery(id+"F2.wireOp",EDGE,"E16.2.0"),sQuery(id+"F2.wireOp",EDGE,"E16.2.1"),sQuery(id+"F2.wireOp",EDGE,"E16.2.2"),sQuery(id+"F2.wireOp",EDGE,"E16.2.3"),sQuery(id+"F2.wireOp",EDGE,"E16.2.4"),sQuery(id+"F2.wireOp",EDGE,"E16.2.5"),sQuery(id+"F2.wireOp",EDGE,"E16.3.0"),sQuery(id+"F2.wireOp",EDGE,"E16.3.1"),sQuery(id+"F2.wireOp",EDGE,"E16.3.2"),sQuery(id+"F2.wireOp",EDGE,"E16.3.3"),sQuery(id+"F2.wireOp",EDGE,"E16.3.4"),sQuery(id+"F2.wireOp",EDGE,"E16.3.5"),sQuery(id+"F2.wireOp",EDGE,"E16.4.0"),sQuery(id+"F2.wireOp",EDGE,"E16.4.1"),sQuery(id+"F2.wireOp",EDGE,"E16.4.2"),sQuery(id+"F2.wireOp",EDGE,"E16.4.3"),sQuery(id+"F2.wireOp",EDGE,"E16.4.4"),sQuery(id+"F2.wireOp",EDGE,"E16.4.5"),sQuery(id+"F2.wireOp",EDGE,"E16.5.0"),sQuery(id+"F2.wireOp",EDGE,"E16.5.1"),sQuery(id+"F2.wireOp",EDGE,"E16.5.2"),sQuery(id+"F2.wireOp",EDGE,"E16.5.3"),sQuery(id+"F2.wireOp",EDGE,"E16.5.4"),sQuery(id+"F2.wireOp",EDGE,"E16.5.5"),sQuery(id+"F2.wireOp",EDGE,"E16.6.0"),sQuery(id+"F2.wireOp",EDGE,"E16.6.1"),sQuery(id+"F2.wireOp",EDGE,"E16.6.2"),sQuery(id+"F2.wireOp",EDGE,"E16.6.3"),sQuery(id+"F2.wireOp",EDGE,"E16.6.4"),sQuery(id+"F2.wireOp",EDGE,"E16.6.5"),sQuery(id+"F2.wireOp",EDGE,"E16.7.0"),sQuery(id+"F2.wireOp",EDGE,"E16.7.1"),sQuery(id+"F2.wireOp",EDGE,"E16.7.2"),sQuery(id+"F2.wireOp",EDGE,"E16.7.3"),sQuery(id+"F2.wireOp",EDGE,"E16.7.4"),sQuery(id+"F2.wireOp",EDGE,"E16.7.5"),sQuery(id+"F2.wireOp",EDGE,"E16.8.0"),sQuery(id+"F2.wireOp",EDGE,"E16.8.1"),sQuery(id+"F2.wireOp",EDGE,"E16.8.2"),sQuery(id+"F2.wireOp",EDGE,"E16.8.3"),sQuery(id+"F2.wireOp",EDGE,"E16.8.4"),sQuery(id+"F2.wireOp",EDGE,"E16.8.5"),sQuery(id+"F2.wireOp",EDGE,"E16.9.0"),sQuery(id+"F2.wireOp",EDGE,"E16.9.1"),sQuery(id+"F2.wireOp",EDGE,"E16.9.2"),sQuery(id+"F2.wireOp",EDGE,"E16.9.3"),sQuery(id+"F2.wireOp",EDGE,"E16.9.4"),sQuery(id+"F2.wireOp",EDGE,"E16.9.5"),sQuery(id+"F2.wireOp",EDGE,"E16.10.0"),sQuery(id+"F2.wireOp",EDGE,"E16.10.1"),sQuery(id+"F2.wireOp",EDGE,"E16.10.2"),sQuery(id+"F2.wireOp",EDGE,"E16.10.3"),sQuery(id+"F2.wireOp",EDGE,"E16.10.4"),sQuery(id+"F2.wireOp",EDGE,"E16.10.5"),sQuery(id+"F2.wireOp",EDGE,"E16.11.0"),sQuery(id+"F2.wireOp",EDGE,"E16.11.1"),sQuery(id+"F2.wireOp",EDGE,"E16.11.2"),sQuery(id+"F2.wireOp",EDGE,"E16.11.3"),sQuery(id+"F2.wireOp",EDGE,"E16.11.4"),sQuery(id+"F2.wireOp",EDGE,"E16.11.5"),sQuery(id+"F2.wireOp",EDGE,"E16.12.0"),sQuery(id+"F2.wireOp",EDGE,"E16.12.1"),sQuery(id+"F2.wireOp",EDGE,"E16.12.2"),sQuery(id+"F2.wireOp",EDGE,"E16.12.3"),sQuery(id+"F2.wireOp",EDGE,"E16.12.4"),sQuery(id+"F2.wireOp",EDGE,"E16.12.5"),sQuery(id+"F2.wireOp",EDGE,"E16.13.0"),sQuery(id+"F2.wireOp",EDGE,"E16.13.1"),sQuery(id+"F2.wireOp",EDGE,"E16.13.2"),sQuery(id+"F2.wireOp",EDGE,"E16.13.3"),sQuery(id+"F2.wireOp",EDGE,"E16.13.4"),sQuery(id+"F2.wireOp",EDGE,"E16.13.5"),sQuery(id+"F2.wireOp",EDGE,"E16.14.0"),sQuery(id+"F2.wireOp",EDGE,"E16.14.1"),sQuery(id+"F2.wireOp",EDGE,"E16.14.2"),sQuery(id+"F2.wireOp",EDGE,"E16.14.3"),sQuery(id+"F2.wireOp",EDGE,"E16.14.4"),sQuery(id+"F2.wireOp",EDGE,"E16.14.5"),sQuery(id+"F2.wireOp",EDGE,"E16.15.0"),sQuery(id+"F2.wireOp",EDGE,"E16.15.1"),sQuery(id+"F2.wireOp",EDGE,"E16.15.2"),sQuery(id+"F2.wireOp",EDGE,"E16.15.3"),sQuery(id+"F2.wireOp",EDGE,"E16.15.4"),sQuery(id+"F2.wireOp",EDGE,"E16.15.5"),sQuery(id+"F2.wireOp",EDGE,"E17.bottom"),sQuery(id+"F2.wireOp",EDGE,"E17.top"),sQuery(id+"F2.wireOp",EDGE,"E17.left"),sQuery(id+"F2.wireOp",EDGE,"E17.right")])],"isStart":false});
            var sketch = newSketch(context, id + "F15", { "sketchPlane" : qUnion([Q0])});
            skLineSegment(sketch, "E52.bottom", {"start": v(4.5, 1.5) * mm, "end": v(-4.5, 1.5) * mm});
            skLineSegment(sketch, "E52.top", {"start": v(4.5, -1.5) * mm, "end": v(-4.5, -1.5) * mm});
            skLineSegment(sketch, "E52.left", {"start": v(4.5, 1.5) * mm, "end": v(4.5, -1.5) * mm});
            skLineSegment(sketch, "E52.right", {"start": v(-4.5, 1.5) * mm, "end": v(-4.5, -1.5) * mm});
            skPoint(sketch, "E52.middle", {"position": v(0, 0) * mm});
            skLineSegment(sketch, "E53.bottom", {"start": v(1.5, 4.5) * mm, "end": v(-1.5, 4.5) * mm});
            skLineSegment(sketch, "E53.top", {"start": v(1.5, -4.5) * mm, "end": v(-1.5, -4.5) * mm});
            skLineSegment(sketch, "E53.left", {"start": v(1.5, 4.5) * mm, "end": v(1.5, -4.5) * mm});
            skLineSegment(sketch, "E53.right", {"start": v(-1.5, 4.5) * mm, "end": v(-1.5, -4.5) * mm});
            skSolve(sketch);
        }
        {
            var Q0;
            Q0 = qSketchRegion(id + "F15", true);
            var Q1;
            Q1=makeQuery(id+"F3.opExtrude","CAP_FACE",FACE,{"disambiguationData":[OSD([sQuery(id+"F2.wireOp",EDGE,"E9.0"),sQuery(id+"F2.wireOp",EDGE,"E10.0"),sQuery(id+"F2.wireOp",EDGE,"E11.0"),sQuery(id+"F2.wireOp",EDGE,"E12.0"),sQuery(id+"F2.wireOp",EDGE,"E14"),sQuery(id+"F2.wireOp",EDGE,"E15"),sQuery(id+"F2.wireOp",EDGE,"E16.1.0"),sQuery(id+"F2.wireOp",EDGE,"E16.1.1"),sQuery(id+"F2.wireOp",EDGE,"E16.1.2"),sQuery(id+"F2.wireOp",EDGE,"E16.1.3"),sQuery(id+"F2.wireOp",EDGE,"E16.1.4"),sQuery(id+"F2.wireOp",EDGE,"E16.1.5"),sQuery(id+"F2.wireOp",EDGE,"E16.2.0"),sQuery(id+"F2.wireOp",EDGE,"E16.2.1"),sQuery(id+"F2.wireOp",EDGE,"E16.2.2"),sQuery(id+"F2.wireOp",EDGE,"E16.2.3"),sQuery(id+"F2.wireOp",EDGE,"E16.2.4"),sQuery(id+"F2.wireOp",EDGE,"E16.2.5"),sQuery(id+"F2.wireOp",EDGE,"E16.3.0"),sQuery(id+"F2.wireOp",EDGE,"E16.3.1"),sQuery(id+"F2.wireOp",EDGE,"E16.3.2"),sQuery(id+"F2.wireOp",EDGE,"E16.3.3"),sQuery(id+"F2.wireOp",EDGE,"E16.3.4"),sQuery(id+"F2.wireOp",EDGE,"E16.3.5"),sQuery(id+"F2.wireOp",EDGE,"E16.4.0"),sQuery(id+"F2.wireOp",EDGE,"E16.4.1"),sQuery(id+"F2.wireOp",EDGE,"E16.4.2"),sQuery(id+"F2.wireOp",EDGE,"E16.4.3"),sQuery(id+"F2.wireOp",EDGE,"E16.4.4"),sQuery(id+"F2.wireOp",EDGE,"E16.4.5"),sQuery(id+"F2.wireOp",EDGE,"E16.5.0"),sQuery(id+"F2.wireOp",EDGE,"E16.5.1"),sQuery(id+"F2.wireOp",EDGE,"E16.5.2"),sQuery(id+"F2.wireOp",EDGE,"E16.5.3"),sQuery(id+"F2.wireOp",EDGE,"E16.5.4"),sQuery(id+"F2.wireOp",EDGE,"E16.5.5"),sQuery(id+"F2.wireOp",EDGE,"E16.6.0"),sQuery(id+"F2.wireOp",EDGE,"E16.6.1"),sQuery(id+"F2.wireOp",EDGE,"E16.6.2"),sQuery(id+"F2.wireOp",EDGE,"E16.6.3"),sQuery(id+"F2.wireOp",EDGE,"E16.6.4"),sQuery(id+"F2.wireOp",EDGE,"E16.6.5"),sQuery(id+"F2.wireOp",EDGE,"E16.7.0"),sQuery(id+"F2.wireOp",EDGE,"E16.7.1"),sQuery(id+"F2.wireOp",EDGE,"E16.7.2"),sQuery(id+"F2.wireOp",EDGE,"E16.7.3"),sQuery(id+"F2.wireOp",EDGE,"E16.7.4"),sQuery(id+"F2.wireOp",EDGE,"E16.7.5"),sQuery(id+"F2.wireOp",EDGE,"E16.8.0"),sQuery(id+"F2.wireOp",EDGE,"E16.8.1"),sQuery(id+"F2.wireOp",EDGE,"E16.8.2"),sQuery(id+"F2.wireOp",EDGE,"E16.8.3"),sQuery(id+"F2.wireOp",EDGE,"E16.8.4"),sQuery(id+"F2.wireOp",EDGE,"E16.8.5"),sQuery(id+"F2.wireOp",EDGE,"E16.9.0"),sQuery(id+"F2.wireOp",EDGE,"E16.9.1"),sQuery(id+"F2.wireOp",EDGE,"E16.9.2"),sQuery(id+"F2.wireOp",EDGE,"E16.9.3"),sQuery(id+"F2.wireOp",EDGE,"E16.9.4"),sQuery(id+"F2.wireOp",EDGE,"E16.9.5"),sQuery(id+"F2.wireOp",EDGE,"E16.10.0"),sQuery(id+"F2.wireOp",EDGE,"E16.10.1"),sQuery(id+"F2.wireOp",EDGE,"E16.10.2"),sQuery(id+"F2.wireOp",EDGE,"E16.10.3"),sQuery(id+"F2.wireOp",EDGE,"E16.10.4"),sQuery(id+"F2.wireOp",EDGE,"E16.10.5"),sQuery(id+"F2.wireOp",EDGE,"E16.11.0"),sQuery(id+"F2.wireOp",EDGE,"E16.11.1"),sQuery(id+"F2.wireOp",EDGE,"E16.11.2"),sQuery(id+"F2.wireOp",EDGE,"E16.11.3"),sQuery(id+"F2.wireOp",EDGE,"E16.11.4"),sQuery(id+"F2.wireOp",EDGE,"E16.11.5"),sQuery(id+"F2.wireOp",EDGE,"E16.12.0"),sQuery(id+"F2.wireOp",EDGE,"E16.12.1"),sQuery(id+"F2.wireOp",EDGE,"E16.12.2"),sQuery(id+"F2.wireOp",EDGE,"E16.12.3"),sQuery(id+"F2.wireOp",EDGE,"E16.12.4"),sQuery(id+"F2.wireOp",EDGE,"E16.12.5"),sQuery(id+"F2.wireOp",EDGE,"E16.13.0"),sQuery(id+"F2.wireOp",EDGE,"E16.13.1"),sQuery(id+"F2.wireOp",EDGE,"E16.13.2"),sQuery(id+"F2.wireOp",EDGE,"E16.13.3"),sQuery(id+"F2.wireOp",EDGE,"E16.13.4"),sQuery(id+"F2.wireOp",EDGE,"E16.13.5"),sQuery(id+"F2.wireOp",EDGE,"E16.14.0"),sQuery(id+"F2.wireOp",EDGE,"E16.14.1"),sQuery(id+"F2.wireOp",EDGE,"E16.14.2"),sQuery(id+"F2.wireOp",EDGE,"E16.14.3"),sQuery(id+"F2.wireOp",EDGE,"E16.14.4"),sQuery(id+"F2.wireOp",EDGE,"E16.14.5"),sQuery(id+"F2.wireOp",EDGE,"E16.15.0"),sQuery(id+"F2.wireOp",EDGE,"E16.15.1"),sQuery(id+"F2.wireOp",EDGE,"E16.15.2"),sQuery(id+"F2.wireOp",EDGE,"E16.15.3"),sQuery(id+"F2.wireOp",EDGE,"E16.15.4"),sQuery(id+"F2.wireOp",EDGE,"E16.15.5"),sQuery(id+"F2.wireOp",EDGE,"E17.bottom"),sQuery(id+"F2.wireOp",EDGE,"E17.top"),sQuery(id+"F2.wireOp",EDGE,"E17.left"),sQuery(id+"F2.wireOp",EDGE,"E17.right")])],"isStart":true});
            extrude(context, id + "F16", {"entities" : qUnion([Q0]), "operationType" : NewBodyOperationType.REMOVE, "endBound" : BoundingType.UP_TO_SURFACE, "oppositeDirection" : true, "depth" : 25 * mm, "endBoundEntityFace" : qUnion([Q1]), "offsetDistance" : 25 * mm});
        }
    });
